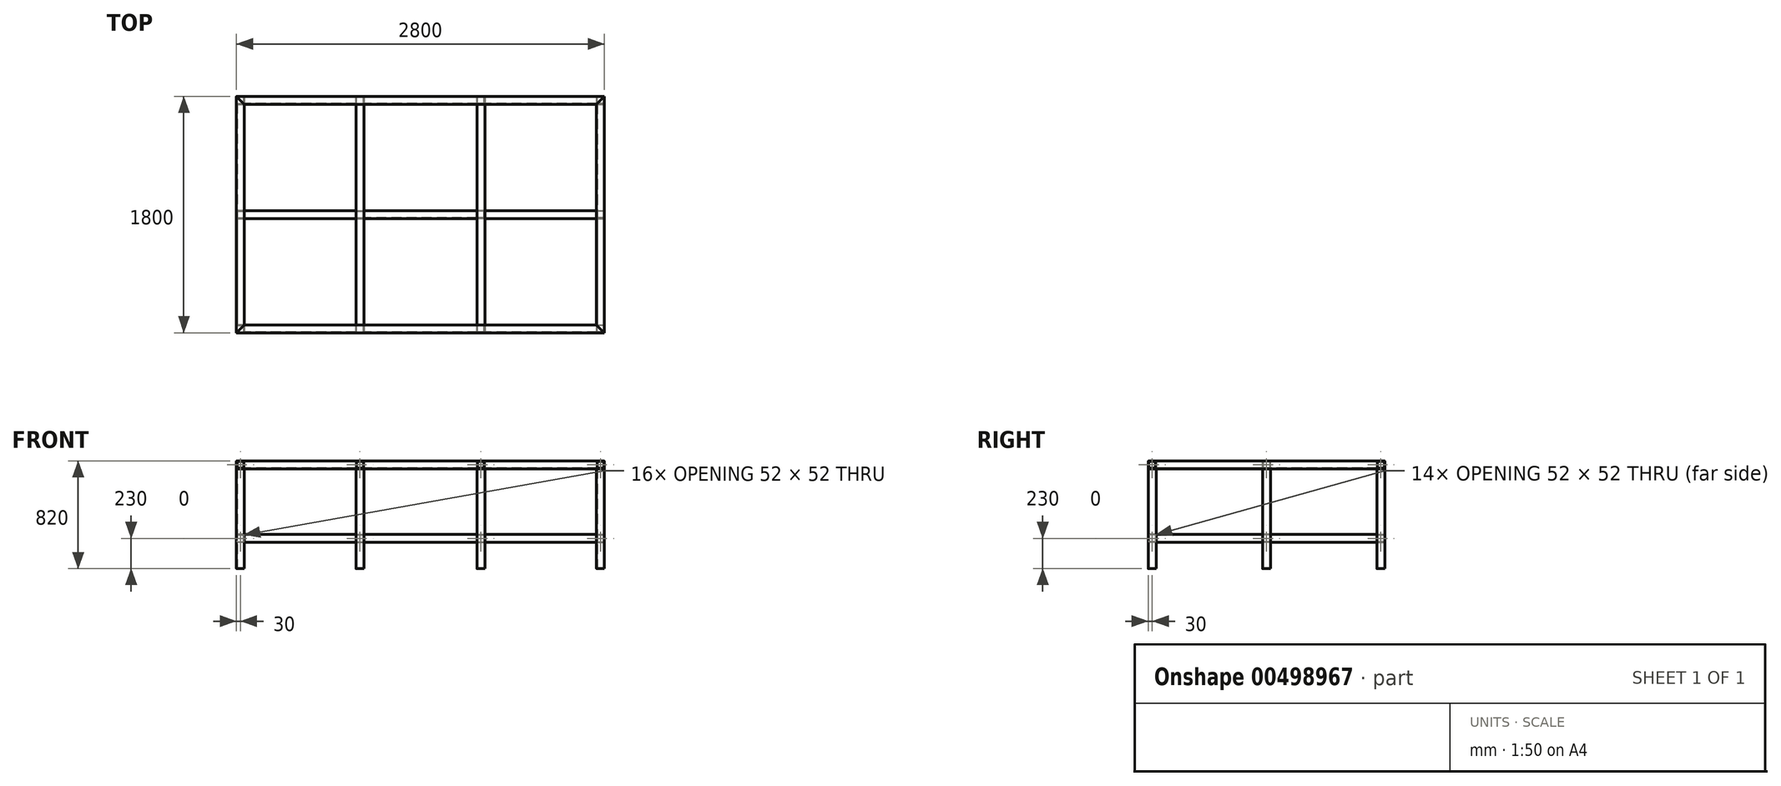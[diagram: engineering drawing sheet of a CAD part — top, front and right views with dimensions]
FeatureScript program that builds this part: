
annotation { "Feature Type Name" : "Feature", "Feature Type Description" : "" }
export const myFeature = defineFeature(function(context is Context, id is Id, definition is map)
    precondition{}
    {
        {
            var Q0;
            Q0=qCreatedBy(makeId("Top.planeOp"),FACE);
            var sketch = newSketch(context, id + "F0", { "sketchPlane" : qUnion([Q0])});
            skLineSegment(sketch, "E0", {"start": v(-1400, 900) * mm, "end": v(1400, 900) * mm});
            skLineSegment(sketch, "E1", {"start": v(-1400, 900) * mm, "end": v(-1340, 840) * mm});
            skLineSegment(sketch, "E2", {"start": v(-1340, 840) * mm, "end": v(1340, 840) * mm});
            skLineSegment(sketch, "E3", {"start": v(1340, 840) * mm, "end": v(1400, 900) * mm});
            skSolve(sketch);
        }
        {
            var Q0;
            Q0 = qSketchRegion(id + "F0", true);
            extrude(context, id + "F1", {"entities" : qUnion([Q0]), "depth" : 60 * mm});
        }
        {
            var Q0;
            Q0=qCreatedBy(makeId("Top.planeOp"),FACE);
            var sketch = newSketch(context, id + "F2", { "sketchPlane" : qUnion([Q0])});
            skLineSegment(sketch, "E4", {"start": v(-1340, 840) * mm, "end": v(-1340, -840) * mm});
            skLineSegment(sketch, "E5", {"start": v(-1340, -840) * mm, "end": v(-1400, -900) * mm});
            skLineSegment(sketch, "E6", {"start": v(-1400, -900) * mm, "end": v(-1400, 900) * mm});
            skLineSegment(sketch, "E7", {"start": v(-1400, 900) * mm, "end": v(-1340, 840) * mm});
            skSolve(sketch);
        }
        {
            var Q0;
            Q0 = qSketchRegion(id + "F2", true);
            extrude(context, id + "F3", {"entities" : qUnion([Q0]), "depth" : 60 * mm});
        }
        {
            var Q0;
            Q0=qCreatedBy(makeId("Top.planeOp"),FACE);
            var sketch = newSketch(context, id + "F4", { "sketchPlane" : qUnion([Q0])});
            skLineSegment(sketch, "E8", {"start": v(-1400, -900) * mm, "end": v(1400, -900) * mm});
            skLineSegment(sketch, "E9", {"start": v(1400, -900) * mm, "end": v(1340, -840) * mm});
            skLineSegment(sketch, "E10", {"start": v(1340, -840) * mm, "end": v(-1340, -840) * mm});
            skLineSegment(sketch, "E11", {"start": v(-1340, -840) * mm, "end": v(-1400, -900) * mm});
            skSolve(sketch);
        }
        {
            var Q0;
            Q0=makeQuery(id+"F4.imprint","IMPRINT",FACE,{"disambiguationData":[TD([[makeQuery(id+"F4.imprint","IMPRINT",EDGE,{"derivedFrom":sQuery(id+"F4.wireOp",EDGE,"E8")}),1.0]])]});
            extrude(context, id + "F5", {"entities" : qUnion([Q0]), "depth" : 60 * mm});
        }
        {
            var Q0;
            Q0=qCreatedBy(makeId("Top.planeOp"),FACE);
            var sketch = newSketch(context, id + "F6", { "sketchPlane" : qUnion([Q0])});
            skLineSegment(sketch, "E12", {"start": v(1400, 900) * mm, "end": v(1400, -900) * mm});
            skLineSegment(sketch, "E13", {"start": v(1400, -900) * mm, "end": v(1340, -840) * mm});
            skLineSegment(sketch, "E14", {"start": v(1340, -840) * mm, "end": v(1340, 840) * mm});
            skLineSegment(sketch, "E15", {"start": v(1340, 840) * mm, "end": v(1400, 900) * mm});
            skSolve(sketch);
        }
        {
            var Q0;
            Q0 = qSketchRegion(id + "F6", true);
            extrude(context, id + "F7", {"entities" : qUnion([Q0]), "depth" : 60 * mm});
        }
        {
            var Q0;
            Q0=makeQuery(id+"F1.opExtrude","SWEPT_FACE",FACE,{"disambiguationData":[OSD([sQuery(id+"F0.wireOp",EDGE,"E2")])]});
            var sketch = newSketch(context, id + "F8", { "sketchPlane" : qUnion([Q0])});
            skLineSegment(sketch, "E16.bottom", {"start": v(-1400, 60) * mm, "end": v(-1340, 60) * mm, "construction": true});
            skLineSegment(sketch, "E16.top", {"start": v(-1400, 0) * mm, "end": v(-1340, 0) * mm, "construction": true});
            skLineSegment(sketch, "E16.left", {"start": v(-1400, 60) * mm, "end": v(-1400, 0) * mm, "construction": true});
            skLineSegment(sketch, "E16.right", {"start": v(-1340, 60) * mm, "end": v(-1340, 0) * mm, "construction": true});
            skLineSegment(sketch, "E17.MirrorCS", {"start": v(1400, 60) * mm, "end": v(1340, 60) * mm, "construction": true});
            skLineSegment(sketch, "E18.MirrorCS", {"start": v(1400, 0) * mm, "end": v(1340, 0) * mm, "construction": true});
            skLineSegment(sketch, "E19.MirrorCS", {"start": v(1400, 60) * mm, "end": v(1400, 0) * mm, "construction": true});
            skLineSegment(sketch, "E20.MirrorCS", {"start": v(1340, 60) * mm, "end": v(1340, 0) * mm, "construction": true});
            skLineSegment(sketch, "E21.bottom", {"start": v(-490, 60) * mm, "end": v(-430, 60) * mm});
            skLineSegment(sketch, "E21.top", {"start": v(-490, 0) * mm, "end": v(-430, 0) * mm});
            skLineSegment(sketch, "E21.left", {"start": v(-490, 60) * mm, "end": v(-490, 0) * mm});
            skLineSegment(sketch, "E21.right", {"start": v(-430, 60) * mm, "end": v(-430, 0) * mm});
            skLineSegment(sketch, "E22.bottom", {"start": v(430, 60) * mm, "end": v(490, 60) * mm});
            skLineSegment(sketch, "E22.top", {"start": v(430, 0) * mm, "end": v(490, 0) * mm});
            skLineSegment(sketch, "E22.left", {"start": v(430, 60) * mm, "end": v(430, 0) * mm});
            skLineSegment(sketch, "E22.right", {"start": v(490, 60) * mm, "end": v(490, 0) * mm});
            skSolve(sketch);
        }
        {
            var Q0;
            Q0 = qSketchRegion(id + "F8", true);
            var Q1;
            Q1=makeQuery(id+"F5.opExtrude","SWEPT_FACE",FACE,{"disambiguationData":[OSD([sQuery(id+"F4.wireOp",EDGE,"E10")])]});
            extrude(context, id + "F9", {"entities" : qUnion([Q0]), "endBound" : BoundingType.UP_TO_SURFACE, "endBoundEntityFace" : qUnion([Q1]), "depth" : 25 * mm});
        }
        {
            var Q0;
            Q0=makeQuery(id+"F3.opExtrude","SWEPT_FACE",FACE,{"disambiguationData":[OSD([sQuery(id+"F2.wireOp",EDGE,"E4")])]});
            var sketch = newSketch(context, id + "F10", { "sketchPlane" : qUnion([Q0])});
            skLineSegment(sketch, "E23.bottom", {"start": v(-30, 60) * mm, "end": v(30, 60) * mm});
            skLineSegment(sketch, "E23.top", {"start": v(-30, 0) * mm, "end": v(30, 0) * mm});
            skLineSegment(sketch, "E23.left", {"start": v(-30, 60) * mm, "end": v(-30, 0) * mm});
            skLineSegment(sketch, "E23.right", {"start": v(30, 60) * mm, "end": v(30, 0) * mm});
            skSolve(sketch);
        }
        {
            var Q0;
            Q0 = qSketchRegion(id + "F10", true);
            extrude(context, id + "F11", {"entities" : qUnion([Q0]), "endBound" : BoundingType.UP_TO_NEXT, "depth" : 25 * mm});
        }
        {
            var Q0;
            Q0=makeQuery(id+"F9.opExtrude","SWEPT_FACE",FACE,{"disambiguationData":[OSD([sQuery(id+"F8.wireOp",EDGE,"E21.right")])]});
            var sketch = newSketch(context, id + "F12", { "sketchPlane" : qUnion([Q0])});
            skSolve(sketch);
        }
        {
            var Q0;
            {var subQ0=sQuery(id+"F8.wireOp",EDGE,"E21.right");Q0=makeQuery(id+"F12.imprint","IMPRINT",FACE,{"disambiguationData":[TD([[makeQuery(id+"F12.imprint","IMPRINT",EDGE,{"derivedFrom":makeQuery(id+"F9.opExtrude","CAP_EDGE",EDGE,{"disambiguationData":[OSD([subQ0])],"isStart":true})}),-1.0]])]});}
            var sketch = newSketch(context, id + "F13", { "sketchPlane" : qUnion([Q0])});
            skLineSegment(sketch, "E24.bottom", {"start": v(-30, 60) * mm, "end": v(30, 60) * mm});
            skLineSegment(sketch, "E24.top", {"start": v(-30, 0) * mm, "end": v(30, 0) * mm});
            skLineSegment(sketch, "E24.left", {"start": v(-30, 60) * mm, "end": v(-30, 0) * mm});
            skLineSegment(sketch, "E24.right", {"start": v(30, 60) * mm, "end": v(30, 0) * mm});
            skSolve(sketch);
        }
        {
            var Q0;
            Q0 = qSketchRegion(id + "F13", true);
            var Q1;
            Q1=makeQuery(id+"F9.opExtrude","SWEPT_FACE",FACE,{"disambiguationData":[OSD([sQuery(id+"F8.wireOp",EDGE,"E22.left")])]});
            extrude(context, id + "F14", {"entities" : qUnion([Q0]), "endBound" : BoundingType.UP_TO_SURFACE, "endBoundEntityFace" : qUnion([Q1]), "depth" : 25 * mm});
        }
        {
            var Q0;
            Q0=makeQuery(id+"F9.opExtrude","SWEPT_FACE",FACE,{"disambiguationData":[OSD([sQuery(id+"F8.wireOp",EDGE,"E22.right")])]});
            var sketch = newSketch(context, id + "F15", { "sketchPlane" : qUnion([Q0])});
            skSolve(sketch);
        }
        {
            var Q0;
            {var subQ0=sQuery(id+"F8.wireOp",EDGE,"E22.right");Q0=makeQuery(id+"F15.imprint","IMPRINT",FACE,{"disambiguationData":[TD([[makeQuery(id+"F15.imprint","IMPRINT",EDGE,{"derivedFrom":makeQuery(id+"F9.opExtrude","CAP_EDGE",EDGE,{"disambiguationData":[OSD([subQ0])],"isStart":true})}),-1.0]])]});}
            var sketch = newSketch(context, id + "F16", { "sketchPlane" : qUnion([Q0])});
            skLineSegment(sketch, "E25.bottom", {"start": v(-30, 60) * mm, "end": v(30, 60) * mm});
            skLineSegment(sketch, "E25.top", {"start": v(-30, 0) * mm, "end": v(30, 0) * mm});
            skLineSegment(sketch, "E25.left", {"start": v(-30, 60) * mm, "end": v(-30, 0) * mm});
            skLineSegment(sketch, "E25.right", {"start": v(30, 60) * mm, "end": v(30, 0) * mm});
            skSolve(sketch);
        }
        {
            var Q0;
            Q0 = qSketchRegion(id + "F16", true);
            var Q1;
            Q1=makeQuery(id+"F7.opExtrude","SWEPT_FACE",FACE,{"disambiguationData":[OSD([sQuery(id+"F6.wireOp",EDGE,"E14")])]});
            extrude(context, id + "F17", {"entities" : qUnion([Q0]), "endBound" : BoundingType.UP_TO_SURFACE, "endBoundEntityFace" : qUnion([Q1]), "depth" : 25 * mm});
        }
        {
            var Q0;
            Q0=makeQuery(id+"F5.opExtrude","CAP_FACE",FACE,{"disambiguationData":[OSD([sQuery(id+"F4.wireOp",EDGE,"E8"),sQuery(id+"F4.wireOp",EDGE,"E9"),sQuery(id+"F4.wireOp",EDGE,"E10"),sQuery(id+"F4.wireOp",EDGE,"E11")])],"isStart":true});
            var sketch = newSketch(context, id + "F18", { "sketchPlane" : qUnion([Q0])});
            skLineSegment(sketch, "E26.bottom", {"start": v(-1340, 840) * mm, "end": v(-1400, 840) * mm});
            skLineSegment(sketch, "E26.top", {"start": v(-1340, 900) * mm, "end": v(-1400, 900) * mm});
            skLineSegment(sketch, "E26.left", {"start": v(-1340, 840) * mm, "end": v(-1340, 900) * mm});
            skLineSegment(sketch, "E26.right", {"start": v(-1400, 840) * mm, "end": v(-1400, 900) * mm});
            skLineSegment(sketch, "E27.bottom", {"start": v(-490, 840) * mm, "end": v(-430, 840) * mm});
            skLineSegment(sketch, "E27.top", {"start": v(-490, 900) * mm, "end": v(-430, 900) * mm});
            skLineSegment(sketch, "E27.left", {"start": v(-490, 840) * mm, "end": v(-490, 900) * mm});
            skLineSegment(sketch, "E27.right", {"start": v(-430, 840) * mm, "end": v(-430, 900) * mm});
            skLineSegment(sketch, "E28.bottom", {"start": v(-1340, 30) * mm, "end": v(-1400, 30) * mm});
            skLineSegment(sketch, "E28.top", {"start": v(-1340, -30) * mm, "end": v(-1400, -30) * mm});
            skLineSegment(sketch, "E28.left", {"start": v(-1340, 30) * mm, "end": v(-1340, -30) * mm});
            skLineSegment(sketch, "E28.right", {"start": v(-1400, 30) * mm, "end": v(-1400, -30) * mm});
            skLineSegment(sketch, "E29.bottom", {"start": v(-490, 30) * mm, "end": v(-430, 30) * mm});
            skLineSegment(sketch, "E29.top", {"start": v(-490, -30) * mm, "end": v(-430, -30) * mm});
            skLineSegment(sketch, "E29.left", {"start": v(-490, 30) * mm, "end": v(-490, -30) * mm});
            skLineSegment(sketch, "E29.right", {"start": v(-430, 30) * mm, "end": v(-430, -30) * mm});
            skLineSegment(sketch, "E30.bottom", {"start": v(-1340, -900) * mm, "end": v(-1400, -900) * mm});
            skLineSegment(sketch, "E30.top", {"start": v(-1340, -840) * mm, "end": v(-1400, -840) * mm});
            skLineSegment(sketch, "E30.left", {"start": v(-1340, -900) * mm, "end": v(-1340, -840) * mm});
            skLineSegment(sketch, "E30.right", {"start": v(-1400, -900) * mm, "end": v(-1400, -840) * mm});
            skLineSegment(sketch, "E31.bottom", {"start": v(-430, -840) * mm, "end": v(-490, -840) * mm});
            skLineSegment(sketch, "E31.top", {"start": v(-430, -900) * mm, "end": v(-490, -900) * mm});
            skLineSegment(sketch, "E31.left", {"start": v(-430, -840) * mm, "end": v(-430, -900) * mm});
            skLineSegment(sketch, "E31.right", {"start": v(-490, -840) * mm, "end": v(-490, -900) * mm});
            skLineSegment(sketch, "E32.MirrorCS", {"start": v(490, 30) * mm, "end": v(430, 30) * mm});
            skLineSegment(sketch, "E33.MirrorCS", {"start": v(1400, 30) * mm, "end": v(1400, -30) * mm});
            skLineSegment(sketch, "E34.MirrorCS", {"start": v(1340, 30) * mm, "end": v(1340, -30) * mm});
            skLineSegment(sketch, "E35.MirrorCS", {"start": v(1340, -30) * mm, "end": v(1400, -30) * mm});
            skLineSegment(sketch, "E36.MirrorCS", {"start": v(430, -840) * mm, "end": v(430, -900) * mm});
            skLineSegment(sketch, "E37.MirrorCS", {"start": v(430, -840) * mm, "end": v(490, -840) * mm});
            skLineSegment(sketch, "E38.MirrorCS", {"start": v(1340, -900) * mm, "end": v(1340, -840) * mm});
            skLineSegment(sketch, "E39.MirrorCS", {"start": v(1340, -900) * mm, "end": v(1400, -900) * mm});
            skLineSegment(sketch, "E40.MirrorCS", {"start": v(1340, 30) * mm, "end": v(1400, 30) * mm});
            skLineSegment(sketch, "E41.MirrorCS", {"start": v(430, 840) * mm, "end": v(430, 900) * mm});
            skLineSegment(sketch, "E42.MirrorCS", {"start": v(490, 840) * mm, "end": v(490, 900) * mm});
            skLineSegment(sketch, "E43.MirrorCS", {"start": v(490, 900) * mm, "end": v(430, 900) * mm});
            skLineSegment(sketch, "E44.MirrorCS", {"start": v(490, 840) * mm, "end": v(430, 840) * mm});
            skLineSegment(sketch, "E45.MirrorCS", {"start": v(1400, 840) * mm, "end": v(1400, 900) * mm});
            skLineSegment(sketch, "E46.MirrorCS", {"start": v(1340, 840) * mm, "end": v(1340, 900) * mm});
            skLineSegment(sketch, "E47.MirrorCS", {"start": v(430, 30) * mm, "end": v(430, -30) * mm});
            skLineSegment(sketch, "E48.MirrorCS", {"start": v(1340, 900) * mm, "end": v(1400, 900) * mm});
            skLineSegment(sketch, "E49.MirrorCS", {"start": v(490, 30) * mm, "end": v(490, -30) * mm});
            skLineSegment(sketch, "E50.MirrorCS", {"start": v(1340, 840) * mm, "end": v(1400, 840) * mm});
            skLineSegment(sketch, "E51.MirrorCS", {"start": v(490, -30) * mm, "end": v(430, -30) * mm});
            skLineSegment(sketch, "E52.MirrorCS", {"start": v(490, -840) * mm, "end": v(490, -900) * mm});
            skLineSegment(sketch, "E53.MirrorCS", {"start": v(430, -900) * mm, "end": v(490, -900) * mm});
            skLineSegment(sketch, "E54.MirrorCS", {"start": v(1400, -900) * mm, "end": v(1400, -840) * mm});
            skLineSegment(sketch, "E55.MirrorCS", {"start": v(1340, -840) * mm, "end": v(1400, -840) * mm});
            skSolve(sketch);
        }
        {
            var Q0;
            Q0 = qSketchRegion(id + "F18", true);
            extrude(context, id + "F19", {"entities" : qUnion([Q0]), "depth" : 760 * mm});
        }
        {
            var Q0;
            Q0=makeQuery(id+"F19.opExtrude","SWEPT_FACE",FACE,{"disambiguationData":[OSD([sQuery(id+"F18.wireOp",EDGE,"E26.top")])]});
            var sketch = newSketch(context, id + "F20", { "sketchPlane" : qUnion([Q0])});
            skLineSegment(sketch, "E56.bottom", {"start": v(-1340, -500) * mm, "end": v(-490, -500) * mm});
            skLineSegment(sketch, "E56.top", {"start": v(-1340, -560) * mm, "end": v(-490, -560) * mm});
            skLineSegment(sketch, "E56.left", {"start": v(-1340, -500) * mm, "end": v(-1340, -560) * mm});
            skLineSegment(sketch, "E56.right", {"start": v(-490, -500) * mm, "end": v(-490, -560) * mm});
            skLineSegment(sketch, "E57.bottom", {"start": v(-430, -500) * mm, "end": v(430, -500) * mm});
            skLineSegment(sketch, "E57.top", {"start": v(-430, -560) * mm, "end": v(430, -560) * mm});
            skLineSegment(sketch, "E57.left", {"start": v(-430, -500) * mm, "end": v(-430, -560) * mm});
            skLineSegment(sketch, "E57.right", {"start": v(430, -500) * mm, "end": v(430, -560) * mm});
            skLineSegment(sketch, "E58.bottom", {"start": v(490, -500) * mm, "end": v(1340, -500) * mm});
            skLineSegment(sketch, "E58.top", {"start": v(490, -560) * mm, "end": v(1340, -560) * mm});
            skLineSegment(sketch, "E58.left", {"start": v(490, -500) * mm, "end": v(490, -560) * mm});
            skLineSegment(sketch, "E58.right", {"start": v(1340, -500) * mm, "end": v(1340, -560) * mm});
            skSolve(sketch);
        }
        {
            var Q0;
            Q0 = qSketchRegion(id + "F20", true);
            extrude(context, id + "F21", {"entities" : qUnion([Q0]), "oppositeDirection" : true, "depth" : 60 * mm});
        }
        {
            var Q0;
            Q0=makeQuery(id+"F19.opExtrude","SWEPT_FACE",FACE,{"disambiguationData":[OSD([sQuery(id+"F18.wireOp",EDGE,"E28.bottom")])]});
            var sketch = newSketch(context, id + "F22", { "sketchPlane" : qUnion([Q0])});
            skLineSegment(sketch, "E59.bottom", {"start": v(-1340, -500) * mm, "end": v(-490, -500) * mm});
            skLineSegment(sketch, "E59.top", {"start": v(-1340, -560) * mm, "end": v(-490, -560) * mm});
            skLineSegment(sketch, "E59.left", {"start": v(-1340, -500) * mm, "end": v(-1340, -560) * mm});
            skLineSegment(sketch, "E59.right", {"start": v(-490, -500) * mm, "end": v(-490, -560) * mm});
            skLineSegment(sketch, "E60.bottom", {"start": v(-430, -500) * mm, "end": v(430, -500) * mm});
            skLineSegment(sketch, "E60.top", {"start": v(-430, -560) * mm, "end": v(430, -560) * mm});
            skLineSegment(sketch, "E60.left", {"start": v(-430, -500) * mm, "end": v(-430, -560) * mm});
            skLineSegment(sketch, "E60.right", {"start": v(430, -500) * mm, "end": v(430, -560) * mm});
            skLineSegment(sketch, "E61.bottom", {"start": v(490, -500) * mm, "end": v(1340, -500) * mm});
            skLineSegment(sketch, "E61.top", {"start": v(490, -560) * mm, "end": v(1340, -560) * mm});
            skLineSegment(sketch, "E61.left", {"start": v(490, -500) * mm, "end": v(490, -560) * mm});
            skLineSegment(sketch, "E61.right", {"start": v(1340, -500) * mm, "end": v(1340, -560) * mm});
            skSolve(sketch);
        }
        {
            var Q0;
            Q0=makeQuery(id+"F22.imprint","IMPRINT",FACE,{"disambiguationData":[TD([[makeQuery(id+"F22.imprint","IMPRINT",EDGE,{"derivedFrom":sQuery(id+"F22.wireOp",EDGE,"E59.bottom")}),-1.0]])]});
            var Q1;
            Q1=makeQuery(id+"F22.imprint","IMPRINT",FACE,{"disambiguationData":[TD([[makeQuery(id+"F22.imprint","IMPRINT",EDGE,{"derivedFrom":sQuery(id+"F22.wireOp",EDGE,"E60.bottom")}),-1.0]])]});
            var Q2;
            Q2=makeQuery(id+"F22.imprint","IMPRINT",FACE,{"disambiguationData":[TD([[makeQuery(id+"F22.imprint","IMPRINT",EDGE,{"derivedFrom":sQuery(id+"F22.wireOp",EDGE,"E61.bottom")}),-1.0]])]});
            extrude(context, id + "F23", {"entities" : qUnion([Q0, Q1, Q2]), "oppositeDirection" : true, "depth" : 60 * mm});
        }
        {
            var Q0;
            Q0=makeQuery(id+"F19.opExtrude","SWEPT_FACE",FACE,{"disambiguationData":[OSD([sQuery(id+"F18.wireOp",EDGE,"E30.bottom")])]});
            var sketch = newSketch(context, id + "F24", { "sketchPlane" : qUnion([Q0])});
            skLineSegment(sketch, "E62.bottom", {"start": v(-1340, -560) * mm, "end": v(-490, -560) * mm});
            skLineSegment(sketch, "E62.top", {"start": v(-1340, -500) * mm, "end": v(-490, -500) * mm});
            skLineSegment(sketch, "E62.left", {"start": v(-1340, -560) * mm, "end": v(-1340, -500) * mm});
            skLineSegment(sketch, "E62.right", {"start": v(-490, -560) * mm, "end": v(-490, -500) * mm});
            skLineSegment(sketch, "E63.bottom", {"start": v(-430, -560) * mm, "end": v(430, -560) * mm});
            skLineSegment(sketch, "E63.top", {"start": v(-430, -500) * mm, "end": v(430, -500) * mm});
            skLineSegment(sketch, "E63.left", {"start": v(-430, -560) * mm, "end": v(-430, -500) * mm});
            skLineSegment(sketch, "E63.right", {"start": v(430, -560) * mm, "end": v(430, -500) * mm});
            skLineSegment(sketch, "E64.bottom", {"start": v(490, -560) * mm, "end": v(1340, -560) * mm});
            skLineSegment(sketch, "E64.top", {"start": v(490, -500) * mm, "end": v(1340, -500) * mm});
            skLineSegment(sketch, "E64.left", {"start": v(490, -560) * mm, "end": v(490, -500) * mm});
            skLineSegment(sketch, "E64.right", {"start": v(1340, -560) * mm, "end": v(1340, -500) * mm});
            skSolve(sketch);
        }
        {
            var Q0;
            Q0 = qSketchRegion(id + "F24", true);
            extrude(context, id + "F25", {"entities" : qUnion([Q0]), "oppositeDirection" : true, "depth" : 60 * mm});
        }
        {
            var Q0;
            Q0=makeQuery(id+"F19.opExtrude","SWEPT_FACE",FACE,{"disambiguationData":[OSD([sQuery(id+"F18.wireOp",EDGE,"E45.MirrorCS")])]});
            var sketch = newSketch(context, id + "F26", { "sketchPlane" : qUnion([Q0])});
            skLineSegment(sketch, "E65.bottom", {"start": v(-840, -500) * mm, "end": v(-30, -500) * mm});
            skLineSegment(sketch, "E65.top", {"start": v(-840, -560) * mm, "end": v(-30, -560) * mm});
            skLineSegment(sketch, "E65.left", {"start": v(-840, -500) * mm, "end": v(-840, -560) * mm});
            skLineSegment(sketch, "E65.right", {"start": v(-30, -500) * mm, "end": v(-30, -560) * mm});
            skLineSegment(sketch, "E66.bottom", {"start": v(30, -500) * mm, "end": v(840, -500) * mm});
            skLineSegment(sketch, "E66.top", {"start": v(30, -560) * mm, "end": v(840, -560) * mm});
            skLineSegment(sketch, "E66.left", {"start": v(30, -500) * mm, "end": v(30, -560) * mm});
            skLineSegment(sketch, "E66.right", {"start": v(840, -500) * mm, "end": v(840, -560) * mm});
            skSolve(sketch);
        }
        {
            var Q0;
            Q0 = qSketchRegion(id + "F26", true);
            extrude(context, id + "F27", {"entities" : qUnion([Q0]), "oppositeDirection" : true, "depth" : 60 * mm});
        }
        {
            var Q0;
            Q0=makeQuery(id+"F19.opExtrude","SWEPT_FACE",FACE,{"disambiguationData":[OSD([sQuery(id+"F18.wireOp",EDGE,"E42.MirrorCS")])]});
            var sketch = newSketch(context, id + "F28", { "sketchPlane" : qUnion([Q0])});
            skLineSegment(sketch, "E67.bottom", {"start": v(-840, -500) * mm, "end": v(-30, -500) * mm});
            skLineSegment(sketch, "E67.top", {"start": v(-840, -560) * mm, "end": v(-30, -560) * mm});
            skLineSegment(sketch, "E67.left", {"start": v(-840, -500) * mm, "end": v(-840, -560) * mm});
            skLineSegment(sketch, "E67.right", {"start": v(-30, -500) * mm, "end": v(-30, -560) * mm});
            skLineSegment(sketch, "E68.bottom", {"start": v(30, -500) * mm, "end": v(840, -500) * mm});
            skLineSegment(sketch, "E68.top", {"start": v(30, -560) * mm, "end": v(840, -560) * mm});
            skLineSegment(sketch, "E68.left", {"start": v(30, -500) * mm, "end": v(30, -560) * mm});
            skLineSegment(sketch, "E68.right", {"start": v(840, -500) * mm, "end": v(840, -560) * mm});
            skSolve(sketch);
        }
        {
            var Q0;
            Q0 = qSketchRegion(id + "F28", true);
            extrude(context, id + "F29", {"entities" : qUnion([Q0]), "oppositeDirection" : true, "depth" : 60 * mm});
        }
        {
            var Q0;
            Q0=makeQuery(id+"F19.opExtrude","SWEPT_FACE",FACE,{"disambiguationData":[OSD([sQuery(id+"F18.wireOp",EDGE,"E27.right")])]});
            var sketch = newSketch(context, id + "F30", { "sketchPlane" : qUnion([Q0])});
            skLineSegment(sketch, "E69.bottom", {"start": v(-840, -500) * mm, "end": v(-30, -500) * mm});
            skLineSegment(sketch, "E69.top", {"start": v(-840, -560) * mm, "end": v(-30, -560) * mm});
            skLineSegment(sketch, "E69.left", {"start": v(-840, -500) * mm, "end": v(-840, -560) * mm});
            skLineSegment(sketch, "E69.right", {"start": v(-30, -500) * mm, "end": v(-30, -560) * mm});
            skLineSegment(sketch, "E70.bottom", {"start": v(30, -500) * mm, "end": v(840, -500) * mm});
            skLineSegment(sketch, "E70.top", {"start": v(30, -560) * mm, "end": v(840, -560) * mm});
            skLineSegment(sketch, "E70.left", {"start": v(30, -500) * mm, "end": v(30, -560) * mm});
            skLineSegment(sketch, "E70.right", {"start": v(840, -500) * mm, "end": v(840, -560) * mm});
            skSolve(sketch);
        }
        {
            var Q0;
            Q0 = qSketchRegion(id + "F30", true);
            extrude(context, id + "F31", {"entities" : qUnion([Q0]), "oppositeDirection" : true, "depth" : 60 * mm});
        }
        {
            var Q0;
            Q0=makeQuery(id+"F19.opExtrude","SWEPT_FACE",FACE,{"disambiguationData":[OSD([sQuery(id+"F18.wireOp",EDGE,"E30.right")])]});
            var sketch = newSketch(context, id + "F32", { "sketchPlane" : qUnion([Q0])});
            skLineSegment(sketch, "E71.bottom", {"start": v(840, -500) * mm, "end": v(30, -500) * mm});
            skLineSegment(sketch, "E71.top", {"start": v(840, -560) * mm, "end": v(30, -560) * mm});
            skLineSegment(sketch, "E71.left", {"start": v(840, -500) * mm, "end": v(840, -560) * mm});
            skLineSegment(sketch, "E71.right", {"start": v(30, -500) * mm, "end": v(30, -560) * mm});
            skLineSegment(sketch, "E72.bottom", {"start": v(-30, -500) * mm, "end": v(-840, -500) * mm});
            skLineSegment(sketch, "E72.top", {"start": v(-30, -560) * mm, "end": v(-840, -560) * mm});
            skLineSegment(sketch, "E72.left", {"start": v(-30, -500) * mm, "end": v(-30, -560) * mm});
            skLineSegment(sketch, "E72.right", {"start": v(-840, -500) * mm, "end": v(-840, -560) * mm});
            skSolve(sketch);
        }
        {
            var Q0;
            Q0 = qSketchRegion(id + "F32", true);
            extrude(context, id + "F33", {"entities" : qUnion([Q0]), "oppositeDirection" : true, "depth" : 60 * mm});
        }
        {
            var Q0;
            Q0=makeQuery(id+"F19.opExtrude","CAP_FACE",FACE,{"disambiguationData":[OSD([sQuery(id+"F18.wireOp",EDGE,"E45.MirrorCS"),sQuery(id+"F18.wireOp",EDGE,"E46.MirrorCS"),sQuery(id+"F18.wireOp",EDGE,"E48.MirrorCS"),sQuery(id+"F18.wireOp",EDGE,"E50.MirrorCS")])],"isStart":false});
            var sketch = newSketch(context, id + "F34", { "sketchPlane" : qUnion([Q0])});
            skLineSegment(sketch, "E73.bottom", {"start": v(1396, 896) * mm, "end": v(1344, 896) * mm});
            skLineSegment(sketch, "E73.top", {"start": v(1396, 844) * mm, "end": v(1344, 844) * mm});
            skLineSegment(sketch, "E73.left", {"start": v(1396, 896) * mm, "end": v(1396, 844) * mm});
            skLineSegment(sketch, "E73.right", {"start": v(1344, 896) * mm, "end": v(1344, 844) * mm});
            skLineSegment(sketch, "E74.bottom", {"start": v(1396, 26) * mm, "end": v(1344, 26) * mm});
            skLineSegment(sketch, "E74.top", {"start": v(1396, -26) * mm, "end": v(1344, -26) * mm});
            skLineSegment(sketch, "E74.left", {"start": v(1396, 26) * mm, "end": v(1396, -26) * mm});
            skLineSegment(sketch, "E74.right", {"start": v(1344, 26) * mm, "end": v(1344, -26) * mm});
            skLineSegment(sketch, "E75.bottom", {"start": v(486, 896) * mm, "end": v(434, 896) * mm});
            skLineSegment(sketch, "E75.top", {"start": v(486, 844) * mm, "end": v(434, 844) * mm});
            skLineSegment(sketch, "E75.left", {"start": v(486, 896) * mm, "end": v(486, 844) * mm});
            skLineSegment(sketch, "E75.right", {"start": v(434, 896) * mm, "end": v(434, 844) * mm});
            skLineSegment(sketch, "E76.bottom", {"start": v(486, 26) * mm, "end": v(434, 26) * mm});
            skLineSegment(sketch, "E76.top", {"start": v(486, -26) * mm, "end": v(434, -26) * mm});
            skLineSegment(sketch, "E76.left", {"start": v(486, 26) * mm, "end": v(486, -26) * mm});
            skLineSegment(sketch, "E76.right", {"start": v(434, 26) * mm, "end": v(434, -26) * mm});
            skLineSegment(sketch, "E77.bottom", {"start": v(486, -844) * mm, "end": v(434, -844) * mm});
            skLineSegment(sketch, "E77.top", {"start": v(486, -896) * mm, "end": v(434, -896) * mm});
            skLineSegment(sketch, "E77.left", {"start": v(486, -844) * mm, "end": v(486, -896) * mm});
            skLineSegment(sketch, "E77.right", {"start": v(434, -844) * mm, "end": v(434, -896) * mm});
            skLineSegment(sketch, "E78.bottom", {"start": v(1396, -844) * mm, "end": v(1344, -844) * mm});
            skLineSegment(sketch, "E78.top", {"start": v(1396, -896) * mm, "end": v(1344, -896) * mm});
            skLineSegment(sketch, "E78.left", {"start": v(1396, -844) * mm, "end": v(1396, -896) * mm});
            skLineSegment(sketch, "E78.right", {"start": v(1344, -844) * mm, "end": v(1344, -896) * mm});
            skLineSegment(sketch, "E79.MirrorCS", {"start": v(-486, -896) * mm, "end": v(-434, -896) * mm});
            skLineSegment(sketch, "E80.MirrorCS", {"start": v(-434, -844) * mm, "end": v(-434, -896) * mm});
            skLineSegment(sketch, "E81.MirrorCS", {"start": v(-486, 896) * mm, "end": v(-434, 896) * mm});
            skLineSegment(sketch, "E82.MirrorCS", {"start": v(-486, 844) * mm, "end": v(-434, 844) * mm});
            skLineSegment(sketch, "E83.MirrorCS", {"start": v(-486, -844) * mm, "end": v(-486, -896) * mm});
            skLineSegment(sketch, "E84.MirrorCS", {"start": v(-1396, -844) * mm, "end": v(-1396, -896) * mm});
            skLineSegment(sketch, "E85.MirrorCS", {"start": v(-1396, 844) * mm, "end": v(-1344, 844) * mm});
            skLineSegment(sketch, "E86.MirrorCS", {"start": v(-486, 896) * mm, "end": v(-486, 844) * mm});
            skLineSegment(sketch, "E87.MirrorCS", {"start": v(-486, -844) * mm, "end": v(-434, -844) * mm});
            skLineSegment(sketch, "E88.MirrorCS", {"start": v(-1396, 26) * mm, "end": v(-1396, -26) * mm});
            skLineSegment(sketch, "E89.MirrorCS", {"start": v(-1396, 896) * mm, "end": v(-1396, 844) * mm});
            skLineSegment(sketch, "E90.MirrorCS", {"start": v(-1396, -896) * mm, "end": v(-1344, -896) * mm});
            skLineSegment(sketch, "E91.MirrorCS", {"start": v(-434, 896) * mm, "end": v(-434, 844) * mm});
            skLineSegment(sketch, "E92.MirrorCS", {"start": v(-1344, 896) * mm, "end": v(-1344, 844) * mm});
            skLineSegment(sketch, "E93.MirrorCS", {"start": v(-486, 26) * mm, "end": v(-486, -26) * mm});
            skLineSegment(sketch, "E94.MirrorCS", {"start": v(-1396, -844) * mm, "end": v(-1344, -844) * mm});
            skLineSegment(sketch, "E95.MirrorCS", {"start": v(-434, 26) * mm, "end": v(-434, -26) * mm});
            skLineSegment(sketch, "E96.MirrorCS", {"start": v(-1344, 26) * mm, "end": v(-1344, -26) * mm});
            skLineSegment(sketch, "E97.MirrorCS", {"start": v(-486, -26) * mm, "end": v(-434, -26) * mm});
            skLineSegment(sketch, "E98.MirrorCS", {"start": v(-1344, -844) * mm, "end": v(-1344, -896) * mm});
            skLineSegment(sketch, "E99.MirrorCS", {"start": v(-1396, -26) * mm, "end": v(-1344, -26) * mm});
            skLineSegment(sketch, "E100.MirrorCS", {"start": v(-1396, 26) * mm, "end": v(-1344, 26) * mm});
            skLineSegment(sketch, "E101.MirrorCS", {"start": v(-1396, 896) * mm, "end": v(-1344, 896) * mm});
            skLineSegment(sketch, "E102.MirrorCS", {"start": v(-486, 26) * mm, "end": v(-434, 26) * mm});
            skSolve(sketch);
        }
        {
            var Q0;
            Q0 = qSketchRegion(id + "F34", true);
            extrude(context, id + "F35", {"entities" : qUnion([Q0]), "operationType" : NewBodyOperationType.REMOVE, "oppositeDirection" : true, "depth" : 760 * mm});
        }
        {
            var Q0;
            Q0=makeQuery(id+"F21.opExtrude","SWEPT_FACE",FACE,{"disambiguationData":[OSD([sQuery(id+"F20.wireOp",EDGE,"E56.left")])]});
            var sketch = newSketch(context, id + "F36", { "sketchPlane" : qUnion([Q0])});
            skLineSegment(sketch, "E103.bottom", {"start": v(844, -504) * mm, "end": v(896, -504) * mm});
            skLineSegment(sketch, "E103.top", {"start": v(844, -556) * mm, "end": v(896, -556) * mm});
            skLineSegment(sketch, "E103.left", {"start": v(844, -504) * mm, "end": v(844, -556) * mm});
            skLineSegment(sketch, "E103.right", {"start": v(896, -504) * mm, "end": v(896, -556) * mm});
            skLineSegment(sketch, "E104.bottom", {"start": v(-26, -504) * mm, "end": v(26, -504) * mm});
            skLineSegment(sketch, "E104.top", {"start": v(-26, -556) * mm, "end": v(26, -556) * mm});
            skLineSegment(sketch, "E104.left", {"start": v(-26, -504) * mm, "end": v(-26, -556) * mm});
            skLineSegment(sketch, "E104.right", {"start": v(26, -504) * mm, "end": v(26, -556) * mm});
            skLineSegment(sketch, "E105.bottom", {"start": v(-896, -504) * mm, "end": v(-844, -504) * mm});
            skLineSegment(sketch, "E105.top", {"start": v(-896, -556) * mm, "end": v(-844, -556) * mm});
            skLineSegment(sketch, "E105.left", {"start": v(-896, -504) * mm, "end": v(-896, -556) * mm});
            skLineSegment(sketch, "E105.right", {"start": v(-844, -504) * mm, "end": v(-844, -556) * mm});
            skSolve(sketch);
        }
        {
            var Q0;
            Q0 = qSketchRegion(id + "F36", true);
            var Q1;
            Q1=makeQuery(id+"F19.opExtrude","SWEPT_FACE",FACE,{"disambiguationData":[OSD([sQuery(id+"F18.wireOp",EDGE,"E27.left")])]});
            extrude(context, id + "F37", {"entities" : qUnion([Q0]), "operationType" : NewBodyOperationType.REMOVE, "endBound" : BoundingType.UP_TO_SURFACE, "oppositeDirection" : true, "endBoundEntityFace" : qUnion([Q1]), "depth" : 25 * mm});
        }
        {
            var Q0;
            Q0=makeQuery(id+"F33.opExtrude","SWEPT_FACE",FACE,{"disambiguationData":[OSD([sQuery(id+"F32.wireOp",EDGE,"E71.left")])]});
            var sketch = newSketch(context, id + "F38", { "sketchPlane" : qUnion([Q0])});
            skLineSegment(sketch, "E106.bottom", {"start": v(-1396, -556) * mm, "end": v(-1344, -556) * mm});
            skLineSegment(sketch, "E106.top", {"start": v(-1396, -504) * mm, "end": v(-1344, -504) * mm});
            skLineSegment(sketch, "E106.left", {"start": v(-1396, -556) * mm, "end": v(-1396, -504) * mm});
            skLineSegment(sketch, "E106.right", {"start": v(-1344, -556) * mm, "end": v(-1344, -504) * mm});
            skSolve(sketch);
        }
        {
            var Q0;
            Q0 = qSketchRegion(id + "F38", true);
            var Q1;
            Q1=makeQuery(id+"F33.opExtrude","SWEPT_FACE",FACE,{"disambiguationData":[OSD([sQuery(id+"F32.wireOp",EDGE,"E71.right")])]});
            extrude(context, id + "F39", {"entities" : qUnion([Q0]), "operationType" : NewBodyOperationType.REMOVE, "endBound" : BoundingType.UP_TO_SURFACE, "oppositeDirection" : true, "endBoundEntityFace" : qUnion([Q1]), "depth" : 25 * mm});
        }
        {
            var Q0;
            Q0=makeQuery(id+"F33.opExtrude","SWEPT_FACE",FACE,{"disambiguationData":[OSD([sQuery(id+"F32.wireOp",EDGE,"E72.right")])]});
            var sketch = newSketch(context, id + "F40", { "sketchPlane" : qUnion([Q0])});
            skLineSegment(sketch, "E107.bottom", {"start": v(1396, -504) * mm, "end": v(1344, -504) * mm});
            skLineSegment(sketch, "E107.top", {"start": v(1396, -556) * mm, "end": v(1344, -556) * mm});
            skLineSegment(sketch, "E107.left", {"start": v(1396, -504) * mm, "end": v(1396, -556) * mm});
            skLineSegment(sketch, "E107.right", {"start": v(1344, -504) * mm, "end": v(1344, -556) * mm});
            skSolve(sketch);
        }
        {
            var Q0;
            Q0 = qSketchRegion(id + "F40", true);
            var Q1;
            Q1=makeQuery(id+"F33.opExtrude","SWEPT_FACE",FACE,{"disambiguationData":[OSD([sQuery(id+"F32.wireOp",EDGE,"E72.left")])]});
            extrude(context, id + "F41", {"entities" : qUnion([Q0]), "operationType" : NewBodyOperationType.REMOVE, "endBound" : BoundingType.UP_TO_SURFACE, "oppositeDirection" : true, "endBoundEntityFace" : qUnion([Q1]), "depth" : 25 * mm});
        }
        {
            var Q0;
            Q0=qCreatedBy(makeId("Front.planeOp"),FACE);
            var sketch = newSketch(context, id + "F42", { "sketchPlane" : qUnion([Q0])});
            skLineSegment(sketch, "E108.bottom", {"start": v(-1396, 56) * mm, "end": v(-1344, 56) * mm});
            skLineSegment(sketch, "E108.top", {"start": v(-1396, 4) * mm, "end": v(-1344, 4) * mm});
            skLineSegment(sketch, "E108.left", {"start": v(-1396, 56) * mm, "end": v(-1396, 4) * mm});
            skLineSegment(sketch, "E108.right", {"start": v(-1344, 56) * mm, "end": v(-1344, 4) * mm});
            skLineSegment(sketch, "E109.bottom", {"start": v(-486, 56) * mm, "end": v(-434, 56) * mm});
            skLineSegment(sketch, "E109.top", {"start": v(-486, 4) * mm, "end": v(-434, 4) * mm});
            skLineSegment(sketch, "E109.left", {"start": v(-486, 56) * mm, "end": v(-486, 4) * mm});
            skLineSegment(sketch, "E109.right", {"start": v(-434, 56) * mm, "end": v(-434, 4) * mm});
            skLineSegment(sketch, "E110.bottom", {"start": v(434, 56) * mm, "end": v(486, 56) * mm});
            skLineSegment(sketch, "E110.top", {"start": v(434, 4) * mm, "end": v(486, 4) * mm});
            skLineSegment(sketch, "E110.left", {"start": v(434, 56) * mm, "end": v(434, 4) * mm});
            skLineSegment(sketch, "E110.right", {"start": v(486, 56) * mm, "end": v(486, 4) * mm});
            skLineSegment(sketch, "E111.bottom", {"start": v(1344, 56) * mm, "end": v(1396, 56) * mm});
            skLineSegment(sketch, "E111.top", {"start": v(1344, 4) * mm, "end": v(1396, 4) * mm});
            skLineSegment(sketch, "E111.left", {"start": v(1344, 56) * mm, "end": v(1344, 4) * mm});
            skLineSegment(sketch, "E111.right", {"start": v(1396, 56) * mm, "end": v(1396, 4) * mm});
            skSolve(sketch);
        }
        {
            var Q0;
            Q0 = qSketchRegion(id + "F42", true);
            extrude(context, id + "F43", {"entities" : qUnion([Q0]), "operationType" : NewBodyOperationType.REMOVE, "endBound" : BoundingType.SYMMETRIC, "oppositeDirection" : true, "depth" : 1800 * mm});
        }
        {
            var Q0;
            Q0=makeQuery(id+"F17.opExtrude","CAP_FACE",FACE,{"disambiguationData":[OSD([sQuery(id+"F16.wireOp",EDGE,"E25.bottom"),sQuery(id+"F16.wireOp",EDGE,"E25.top"),sQuery(id+"F16.wireOp",EDGE,"E25.left"),sQuery(id+"F16.wireOp",EDGE,"E25.right")])],"isStart":false});
            var sketch = newSketch(context, id + "F44", { "sketchPlane" : qUnion([Q0])});
            skLineSegment(sketch, "E112.bottom", {"start": v(-26, 56) * mm, "end": v(26, 56) * mm});
            skLineSegment(sketch, "E112.top", {"start": v(-26, 4) * mm, "end": v(26, 4) * mm});
            skLineSegment(sketch, "E112.left", {"start": v(-26, 56) * mm, "end": v(-26, 4) * mm});
            skLineSegment(sketch, "E112.right", {"start": v(26, 56) * mm, "end": v(26, 4) * mm});
            skSolve(sketch);
        }
        {
            var Q0;
            Q0 = qSketchRegion(id + "F44", true);
            var Q1;
            Q1=makeQuery(id+"F3.opExtrude","SWEPT_FACE",FACE,{"disambiguationData":[OSD([sQuery(id+"F2.wireOp",EDGE,"E4")])]});
            extrude(context, id + "F45", {"entities" : qUnion([Q0]), "operationType" : NewBodyOperationType.REMOVE, "endBound" : BoundingType.UP_TO_SURFACE, "oppositeDirection" : true, "endBoundEntityFace" : qUnion([Q1]), "depth" : 25 * mm});
        }
        {
            var Q0;
            Q0=makeQuery(id+"F31.opExtrude","SWEPT_FACE",FACE,{"disambiguationData":[OSD([sQuery(id+"F30.wireOp",EDGE,"E69.left")])]});
            var sketch = newSketch(context, id + "F46", { "sketchPlane" : qUnion([Q0])});
            skLineSegment(sketch, "E113.bottom", {"start": v(-486, -504) * mm, "end": v(-434, -504) * mm});
            skLineSegment(sketch, "E113.top", {"start": v(-486, -556) * mm, "end": v(-434, -556) * mm});
            skLineSegment(sketch, "E113.left", {"start": v(-486, -504) * mm, "end": v(-486, -556) * mm});
            skLineSegment(sketch, "E113.right", {"start": v(-434, -504) * mm, "end": v(-434, -556) * mm});
            skLineSegment(sketch, "E114.bottom", {"start": v(434, -504) * mm, "end": v(486, -504) * mm});
            skLineSegment(sketch, "E114.top", {"start": v(434, -556) * mm, "end": v(486, -556) * mm});
            skLineSegment(sketch, "E114.left", {"start": v(434, -504) * mm, "end": v(434, -556) * mm});
            skLineSegment(sketch, "E114.right", {"start": v(486, -504) * mm, "end": v(486, -556) * mm});
            skLineSegment(sketch, "E115.bottom", {"start": v(1344, -504) * mm, "end": v(1396, -504) * mm});
            skLineSegment(sketch, "E115.top", {"start": v(1344, -556) * mm, "end": v(1396, -556) * mm});
            skLineSegment(sketch, "E115.left", {"start": v(1344, -504) * mm, "end": v(1344, -556) * mm});
            skLineSegment(sketch, "E115.right", {"start": v(1396, -504) * mm, "end": v(1396, -556) * mm});
            skSolve(sketch);
        }
        {
            var Q0;
            Q0 = qSketchRegion(id + "F46", true);
            var Q1;
            Q1=makeQuery(id+"F23.opExtrude","CAP_FACE",FACE,{"disambiguationData":[OSD([sQuery(id+"F22.wireOp",EDGE,"E60.bottom"),sQuery(id+"F22.wireOp",EDGE,"E60.top"),sQuery(id+"F22.wireOp",EDGE,"E60.left"),sQuery(id+"F22.wireOp",EDGE,"E60.right")])],"isStart":true});
            extrude(context, id + "F47", {"entities" : qUnion([Q0]), "operationType" : NewBodyOperationType.REMOVE, "endBound" : BoundingType.UP_TO_SURFACE, "oppositeDirection" : true, "endBoundEntityFace" : qUnion([Q1]), "depth" : 25 * mm});
        }
        {
            var Q0;
            Q0=makeQuery(id+"F31.opExtrude","SWEPT_FACE",FACE,{"disambiguationData":[OSD([sQuery(id+"F30.wireOp",EDGE,"E70.left")])]});
            var sketch = newSketch(context, id + "F48", { "sketchPlane" : qUnion([Q0])});
            skLineSegment(sketch, "E116.bottom", {"start": v(-486, -504) * mm, "end": v(-434, -504) * mm});
            skLineSegment(sketch, "E116.top", {"start": v(-486, -556) * mm, "end": v(-434, -556) * mm});
            skLineSegment(sketch, "E116.left", {"start": v(-486, -504) * mm, "end": v(-486, -556) * mm});
            skLineSegment(sketch, "E116.right", {"start": v(-434, -504) * mm, "end": v(-434, -556) * mm});
            skLineSegment(sketch, "E117.bottom", {"start": v(434, -504) * mm, "end": v(486, -504) * mm});
            skLineSegment(sketch, "E117.top", {"start": v(434, -556) * mm, "end": v(486, -556) * mm});
            skLineSegment(sketch, "E117.left", {"start": v(434, -504) * mm, "end": v(434, -556) * mm});
            skLineSegment(sketch, "E117.right", {"start": v(486, -504) * mm, "end": v(486, -556) * mm});
            skLineSegment(sketch, "E118.bottom", {"start": v(1344, -504) * mm, "end": v(1396, -504) * mm});
            skLineSegment(sketch, "E118.top", {"start": v(1344, -556) * mm, "end": v(1396, -556) * mm});
            skLineSegment(sketch, "E118.left", {"start": v(1344, -504) * mm, "end": v(1344, -556) * mm});
            skLineSegment(sketch, "E118.right", {"start": v(1396, -504) * mm, "end": v(1396, -556) * mm});
            skSolve(sketch);
        }
        {
            var Q0;
            Q0 = qSketchRegion(id + "F48", true);
            extrude(context, id + "F49", {"entities" : qUnion([Q0]), "operationType" : NewBodyOperationType.REMOVE, "endBound" : BoundingType.UP_TO_NEXT, "oppositeDirection" : true, "depth" : 25 * mm});
        }
        {
            var Q0;
            Q0=makeQuery(id+"F23.opExtrude","SWEPT_FACE",FACE,{"disambiguationData":[OSD([sQuery(id+"F22.wireOp",EDGE,"E60.left")])]});
            var sketch = newSketch(context, id + "F50", { "sketchPlane" : qUnion([Q0])});
            skLineSegment(sketch, "E119.bottom", {"start": v(-26, -504) * mm, "end": v(26, -504) * mm});
            skLineSegment(sketch, "E119.top", {"start": v(-26, -556) * mm, "end": v(26, -556) * mm});
            skLineSegment(sketch, "E119.left", {"start": v(-26, -504) * mm, "end": v(-26, -556) * mm});
            skLineSegment(sketch, "E119.right", {"start": v(26, -504) * mm, "end": v(26, -556) * mm});
            skSolve(sketch);
        }
        {
            var Q0;
            Q0=makeQuery(id+"F50.imprint","IMPRINT",FACE,{"disambiguationData":[TD([[makeQuery(id+"F50.imprint","IMPRINT",EDGE,{"derivedFrom":sQuery(id+"F50.wireOp",EDGE,"E119.bottom")}),-1.0]])]});
            extrude(context, id + "F51", {"entities" : qUnion([Q0]), "operationType" : NewBodyOperationType.REMOVE, "endBound" : BoundingType.UP_TO_NEXT, "oppositeDirection" : true, "depth" : 25 * mm});
        }
        {
            var Q0;
            Q0=makeQuery(id+"F23.opExtrude","SWEPT_FACE",FACE,{"disambiguationData":[OSD([sQuery(id+"F22.wireOp",EDGE,"E61.right")])]});
            var sketch = newSketch(context, id + "F52", { "sketchPlane" : qUnion([Q0])});
            skLineSegment(sketch, "E120.bottom", {"start": v(26, -504) * mm, "end": v(-26, -504) * mm});
            skLineSegment(sketch, "E120.top", {"start": v(26, -556) * mm, "end": v(-26, -556) * mm});
            skLineSegment(sketch, "E120.left", {"start": v(26, -504) * mm, "end": v(26, -556) * mm});
            skLineSegment(sketch, "E120.right", {"start": v(-26, -504) * mm, "end": v(-26, -556) * mm});
            skSolve(sketch);
        }
        {
            var Q0;
            Q0 = qSketchRegion(id + "F52", true);
            extrude(context, id + "F53", {"entities" : qUnion([Q0]), "operationType" : NewBodyOperationType.REMOVE, "endBound" : BoundingType.UP_TO_NEXT, "oppositeDirection" : true, "depth" : 25 * mm});
        }
        {
            var Q0;
            Q0=makeQuery(id+"F21.opExtrude","SWEPT_FACE",FACE,{"disambiguationData":[OSD([sQuery(id+"F20.wireOp",EDGE,"E57.right")])]});
            var sketch = newSketch(context, id + "F54", { "sketchPlane" : qUnion([Q0])});
            skLineSegment(sketch, "E121.bottom", {"start": v(-896, -504) * mm, "end": v(-844, -504) * mm});
            skLineSegment(sketch, "E121.top", {"start": v(-896, -556) * mm, "end": v(-844, -556) * mm});
            skLineSegment(sketch, "E121.left", {"start": v(-896, -504) * mm, "end": v(-896, -556) * mm});
            skLineSegment(sketch, "E121.right", {"start": v(-844, -504) * mm, "end": v(-844, -556) * mm});
            skSolve(sketch);
        }
        {
            var Q0;
            Q0 = qSketchRegion(id + "F54", true);
            extrude(context, id + "F55", {"entities" : qUnion([Q0]), "operationType" : NewBodyOperationType.REMOVE, "endBound" : BoundingType.UP_TO_NEXT, "oppositeDirection" : true, "depth" : 25 * mm});
        }
        {
            var Q0;
            Q0=makeQuery(id+"F21.opExtrude","SWEPT_FACE",FACE,{"disambiguationData":[OSD([sQuery(id+"F20.wireOp",EDGE,"E58.right")])]});
            var sketch = newSketch(context, id + "F56", { "sketchPlane" : qUnion([Q0])});
            skLineSegment(sketch, "E122.bottom", {"start": v(-844, -504) * mm, "end": v(-896, -504) * mm});
            skLineSegment(sketch, "E122.top", {"start": v(-844, -556) * mm, "end": v(-896, -556) * mm});
            skLineSegment(sketch, "E122.left", {"start": v(-844, -504) * mm, "end": v(-844, -556) * mm});
            skLineSegment(sketch, "E122.right", {"start": v(-896, -504) * mm, "end": v(-896, -556) * mm});
            skSolve(sketch);
        }
        {
            var Q0;
            Q0 = qSketchRegion(id + "F56", true);
            extrude(context, id + "F57", {"entities" : qUnion([Q0]), "operationType" : NewBodyOperationType.REMOVE, "endBound" : BoundingType.UP_TO_NEXT, "oppositeDirection" : true, "depth" : 25 * mm});
        }
        {
            var Q0;
            Q0=makeQuery(id+"F25.opExtrude","SWEPT_FACE",FACE,{"disambiguationData":[OSD([sQuery(id+"F24.wireOp",EDGE,"E62.left")])]});
            var sketch = newSketch(context, id + "F58", { "sketchPlane" : qUnion([Q0])});
            skLineSegment(sketch, "E123.bottom", {"start": v(896, -504) * mm, "end": v(844, -504) * mm});
            skLineSegment(sketch, "E123.top", {"start": v(896, -556) * mm, "end": v(844, -556) * mm});
            skLineSegment(sketch, "E123.left", {"start": v(896, -504) * mm, "end": v(896, -556) * mm});
            skLineSegment(sketch, "E123.right", {"start": v(844, -504) * mm, "end": v(844, -556) * mm});
            skSolve(sketch);
        }
        {
            var Q0;
            Q0 = qSketchRegion(id + "F58", true);
            var Q1;
            Q1=makeQuery(id+"F25.opExtrude","SWEPT_FACE",FACE,{"disambiguationData":[OSD([sQuery(id+"F24.wireOp",EDGE,"E63.right")])]});
            extrude(context, id + "F59", {"entities" : qUnion([Q0]), "operationType" : NewBodyOperationType.REMOVE, "endBound" : BoundingType.UP_TO_SURFACE, "oppositeDirection" : true, "endBoundEntityFace" : qUnion([Q1]), "depth" : 25 * mm});
        }
        {
            var Q0;
            Q0=makeQuery(id+"F19.opExtrude","SWEPT_EDGE",EDGE,{"disambiguationData":[OSD([sQuery(id+"F4.wireOp",EDGE,"E9"),sQuery(id+"F18.wireOp",EDGE,"E45.MirrorCS"),sQuery(id+"F18.wireOp",EDGE,"E48.MirrorCS")])]});
            var Q1;
            Q1=makeQuery(id+"F19.opExtrude","SWEPT_EDGE",EDGE,{"disambiguationData":[OSD([sQuery(id+"F4.wireOp",EDGE,"E8"),sQuery(id+"F18.wireOp",EDGE,"E46.MirrorCS"),sQuery(id+"F18.wireOp",EDGE,"E48.MirrorCS")])]});
            var Q2;
            Q2=makeQuery(id+"F19.opExtrude","SWEPT_EDGE",EDGE,{"disambiguationData":[OSD([sQuery(id+"F18.wireOp",EDGE,"E45.MirrorCS"),sQuery(id+"F18.wireOp",EDGE,"E50.MirrorCS")])]});
            var Q3;
            Q3=makeQuery(id+"F19.opExtrude","SWEPT_EDGE",EDGE,{"disambiguationData":[OSD([sQuery(id+"F4.wireOp",EDGE,"E9"),sQuery(id+"F4.wireOp",EDGE,"E10"),sQuery(id+"F18.wireOp",EDGE,"E46.MirrorCS"),sQuery(id+"F18.wireOp",EDGE,"E50.MirrorCS")])]});
            var Q4;
            Q4=makeQuery(id+"F19.opExtrude","SWEPT_EDGE",EDGE,{"disambiguationData":[OSD([sQuery(id+"F18.wireOp",EDGE,"E34.MirrorCS"),sQuery(id+"F18.wireOp",EDGE,"E35.MirrorCS")])]});
            var Q5;
            Q5=makeQuery(id+"F19.opExtrude","SWEPT_EDGE",EDGE,{"disambiguationData":[OSD([sQuery(id+"F18.wireOp",EDGE,"E33.MirrorCS"),sQuery(id+"F18.wireOp",EDGE,"E35.MirrorCS")])]});
            var Q6;
            Q6=makeQuery(id+"F19.opExtrude","SWEPT_EDGE",EDGE,{"disambiguationData":[OSD([sQuery(id+"F18.wireOp",EDGE,"E34.MirrorCS"),sQuery(id+"F18.wireOp",EDGE,"E40.MirrorCS")])]});
            var Q7;
            Q7=makeQuery(id+"F19.opExtrude","SWEPT_EDGE",EDGE,{"disambiguationData":[OSD([sQuery(id+"F18.wireOp",EDGE,"E38.MirrorCS"),sQuery(id+"F18.wireOp",EDGE,"E55.MirrorCS")])]});
            var Q8;
            Q8=makeQuery(id+"F19.opExtrude","SWEPT_EDGE",EDGE,{"disambiguationData":[OSD([sQuery(id+"F18.wireOp",EDGE,"E38.MirrorCS"),sQuery(id+"F18.wireOp",EDGE,"E39.MirrorCS")])]});
            var Q9;
            Q9=makeQuery(id+"F19.opExtrude","SWEPT_EDGE",EDGE,{"disambiguationData":[OSD([sQuery(id+"F18.wireOp",EDGE,"E39.MirrorCS"),sQuery(id+"F18.wireOp",EDGE,"E54.MirrorCS")])]});
            var Q10;
            Q10=makeQuery(id+"F19.opExtrude","SWEPT_EDGE",EDGE,{"disambiguationData":[OSD([sQuery(id+"F18.wireOp",EDGE,"E54.MirrorCS"),sQuery(id+"F18.wireOp",EDGE,"E55.MirrorCS")])]});
            var Q11;
            Q11=makeQuery(id+"F19.opExtrude","SWEPT_EDGE",EDGE,{"disambiguationData":[OSD([sQuery(id+"F18.wireOp",EDGE,"E33.MirrorCS"),sQuery(id+"F18.wireOp",EDGE,"E40.MirrorCS")])]});
            var Q12;
            Q12=makeQuery(id+"F19.opExtrude","SWEPT_EDGE",EDGE,{"disambiguationData":[OSD([sQuery(id+"F4.wireOp",EDGE,"E10"),sQuery(id+"F18.wireOp",EDGE,"E41.MirrorCS"),sQuery(id+"F18.wireOp",EDGE,"E44.MirrorCS")])]});
            var Q13;
            Q13=makeQuery(id+"F19.opExtrude","SWEPT_EDGE",EDGE,{"disambiguationData":[OSD([sQuery(id+"F4.wireOp",EDGE,"E10"),sQuery(id+"F18.wireOp",EDGE,"E42.MirrorCS"),sQuery(id+"F18.wireOp",EDGE,"E44.MirrorCS")])]});
            var Q14;
            Q14=makeQuery(id+"F19.opExtrude","SWEPT_EDGE",EDGE,{"disambiguationData":[OSD([sQuery(id+"F4.wireOp",EDGE,"E8"),sQuery(id+"F18.wireOp",EDGE,"E42.MirrorCS"),sQuery(id+"F18.wireOp",EDGE,"E43.MirrorCS")])]});
            var Q15;
            Q15=makeQuery(id+"F19.opExtrude","SWEPT_EDGE",EDGE,{"disambiguationData":[OSD([sQuery(id+"F18.wireOp",EDGE,"E47.MirrorCS"),sQuery(id+"F18.wireOp",EDGE,"E51.MirrorCS")])]});
            var Q16;
            Q16=makeQuery(id+"F19.opExtrude","SWEPT_EDGE",EDGE,{"disambiguationData":[OSD([sQuery(id+"F18.wireOp",EDGE,"E49.MirrorCS"),sQuery(id+"F18.wireOp",EDGE,"E51.MirrorCS")])]});
            var Q17;
            Q17=makeQuery(id+"F19.opExtrude","SWEPT_EDGE",EDGE,{"disambiguationData":[OSD([sQuery(id+"F18.wireOp",EDGE,"E32.MirrorCS"),sQuery(id+"F18.wireOp",EDGE,"E49.MirrorCS")])]});
            var Q18;
            Q18=makeQuery(id+"F19.opExtrude","SWEPT_EDGE",EDGE,{"disambiguationData":[OSD([sQuery(id+"F18.wireOp",EDGE,"E36.MirrorCS"),sQuery(id+"F18.wireOp",EDGE,"E53.MirrorCS")])]});
            var Q19;
            Q19=makeQuery(id+"F19.opExtrude","SWEPT_EDGE",EDGE,{"disambiguationData":[OSD([sQuery(id+"F18.wireOp",EDGE,"E52.MirrorCS"),sQuery(id+"F18.wireOp",EDGE,"E53.MirrorCS")])]});
            var Q20;
            Q20=makeQuery(id+"F19.opExtrude","SWEPT_EDGE",EDGE,{"disambiguationData":[OSD([sQuery(id+"F18.wireOp",EDGE,"E37.MirrorCS"),sQuery(id+"F18.wireOp",EDGE,"E52.MirrorCS")])]});
            var Q21;
            Q21=makeQuery(id+"F19.opExtrude","SWEPT_EDGE",EDGE,{"disambiguationData":[OSD([sQuery(id+"F18.wireOp",EDGE,"E31.top"),sQuery(id+"F18.wireOp",EDGE,"E31.right")])]});
            var Q22;
            Q22=makeQuery(id+"F19.opExtrude","SWEPT_EDGE",EDGE,{"disambiguationData":[OSD([sQuery(id+"F18.wireOp",EDGE,"E31.top"),sQuery(id+"F18.wireOp",EDGE,"E31.left")])]});
            var Q23;
            Q23=makeQuery(id+"F19.opExtrude","SWEPT_EDGE",EDGE,{"disambiguationData":[OSD([sQuery(id+"F18.wireOp",EDGE,"E31.bottom"),sQuery(id+"F18.wireOp",EDGE,"E31.left")])]});
            var Q24;
            Q24=makeQuery(id+"F19.opExtrude","SWEPT_EDGE",EDGE,{"disambiguationData":[OSD([sQuery(id+"F18.wireOp",EDGE,"E30.bottom"),sQuery(id+"F18.wireOp",EDGE,"E30.right")])]});
            var Q25;
            Q25=makeQuery(id+"F19.opExtrude","SWEPT_EDGE",EDGE,{"disambiguationData":[OSD([sQuery(id+"F18.wireOp",EDGE,"E30.bottom"),sQuery(id+"F18.wireOp",EDGE,"E30.left")])]});
            var Q26;
            Q26=makeQuery(id+"F19.opExtrude","SWEPT_EDGE",EDGE,{"disambiguationData":[OSD([sQuery(id+"F18.wireOp",EDGE,"E30.top"),sQuery(id+"F18.wireOp",EDGE,"E30.left")])]});
            fillet(context, id + "F60", {"entities" : qUnion([Q0, Q1, Q2, Q3, Q4, Q5, Q6, Q7, Q8, Q9, Q10, Q11, Q12, Q13, Q14, Q15, Q16, Q17, Q18, Q19, Q20, Q21, Q22, Q23, Q24, Q25, Q26]), "radius" : 3 * mm, "tangentPropagation" : true, "allowEdgeOverflow" : false});
        }
        {
            var Q0;
            Q0=makeQuery(id+"F21.opExtrude","CAP_EDGE",EDGE,{"disambiguationData":[OSD([sQuery(id+"F20.wireOp",EDGE,"E58.bottom")])],"isStart":false});
            var Q1;
            Q1=makeQuery(id+"F21.opExtrude","CAP_EDGE",EDGE,{"disambiguationData":[OSD([sQuery(id+"F20.wireOp",EDGE,"E58.bottom")])],"isStart":true});
            var Q2;
            Q2=makeQuery(id+"F21.opExtrude","CAP_EDGE",EDGE,{"disambiguationData":[OSD([sQuery(id+"F20.wireOp",EDGE,"E58.top")])],"isStart":true});
            var Q3;
            Q3=makeQuery(id+"F21.opExtrude","CAP_EDGE",EDGE,{"disambiguationData":[OSD([sQuery(id+"F20.wireOp",EDGE,"E58.top")])],"isStart":false});
            var Q4;
            Q4=makeQuery(id+"F17.opExtrude","SWEPT_EDGE",EDGE,{"disambiguationData":[OSD([sQuery(id+"F0.wireOp",EDGE,"E2"),sQuery(id+"F8.wireOp",EDGE,"E22.top"),sQuery(id+"F8.wireOp",EDGE,"E22.right"),sQuery(id+"F16.wireOp",EDGE,"E25.top"),sQuery(id+"F16.wireOp",EDGE,"E25.left")])]});
            var Q5;
            Q5=makeQuery(id+"F17.opExtrude","SWEPT_EDGE",EDGE,{"disambiguationData":[OSD([sQuery(id+"F0.wireOp",EDGE,"E2"),sQuery(id+"F8.wireOp",EDGE,"E22.bottom"),sQuery(id+"F8.wireOp",EDGE,"E22.right"),sQuery(id+"F16.wireOp",EDGE,"E25.bottom"),sQuery(id+"F16.wireOp",EDGE,"E25.left")])]});
            var Q6;
            Q6=makeQuery(id+"F17.opExtrude","SWEPT_EDGE",EDGE,{"disambiguationData":[OSD([sQuery(id+"F0.wireOp",EDGE,"E2"),sQuery(id+"F8.wireOp",EDGE,"E22.top"),sQuery(id+"F8.wireOp",EDGE,"E22.right"),sQuery(id+"F16.wireOp",EDGE,"E25.top"),sQuery(id+"F16.wireOp",EDGE,"E25.right")])]});
            var Q7;
            Q7=makeQuery(id+"F23.opExtrude","CAP_EDGE",EDGE,{"disambiguationData":[OSD([sQuery(id+"F22.wireOp",EDGE,"E61.bottom")])],"isStart":true});
            var Q8;
            Q8=makeQuery(id+"F23.opExtrude","CAP_EDGE",EDGE,{"disambiguationData":[OSD([sQuery(id+"F22.wireOp",EDGE,"E61.top")])],"isStart":true});
            var Q9;
            Q9=makeQuery(id+"F23.opExtrude","CAP_EDGE",EDGE,{"disambiguationData":[OSD([sQuery(id+"F22.wireOp",EDGE,"E61.top")])],"isStart":false});
            var Q10;
            Q10=makeQuery(id+"F1.opExtrude","CAP_EDGE",EDGE,{"disambiguationData":[OSD([sQuery(id+"F0.wireOp",EDGE,"E2")])],"isStart":false});
            var Q11;
            Q11=makeQuery(id+"F1.opExtrude","CAP_EDGE",EDGE,{"disambiguationData":[OSD([sQuery(id+"F0.wireOp",EDGE,"E2")])],"isStart":true});
            var Q12;
            Q12=makeQuery(id+"F1.opExtrude","CAP_EDGE",EDGE,{"disambiguationData":[OSD([sQuery(id+"F0.wireOp",EDGE,"E0")])],"isStart":true});
            var Q13;
            Q13=makeQuery(id+"F25.opExtrude","CAP_EDGE",EDGE,{"disambiguationData":[OSD([sQuery(id+"F24.wireOp",EDGE,"E62.top")])],"isStart":false});
            var Q14;
            Q14=makeQuery(id+"F25.opExtrude","CAP_EDGE",EDGE,{"disambiguationData":[OSD([sQuery(id+"F24.wireOp",EDGE,"E62.bottom")])],"isStart":false});
            var Q15;
            Q15=makeQuery(id+"F25.opExtrude","CAP_EDGE",EDGE,{"disambiguationData":[OSD([sQuery(id+"F24.wireOp",EDGE,"E62.bottom")])],"isStart":true});
            var Q16;
            Q16=makeQuery(id+"F25.opExtrude","CAP_EDGE",EDGE,{"disambiguationData":[OSD([sQuery(id+"F24.wireOp",EDGE,"E63.top")])],"isStart":false});
            var Q17;
            Q17=makeQuery(id+"F25.opExtrude","CAP_EDGE",EDGE,{"disambiguationData":[OSD([sQuery(id+"F24.wireOp",EDGE,"E63.bottom")])],"isStart":false});
            var Q18;
            Q18=makeQuery(id+"F25.opExtrude","CAP_EDGE",EDGE,{"disambiguationData":[OSD([sQuery(id+"F24.wireOp",EDGE,"E64.bottom")])],"isStart":true});
            var Q19;
            Q19=makeQuery(id+"F25.opExtrude","CAP_EDGE",EDGE,{"disambiguationData":[OSD([sQuery(id+"F24.wireOp",EDGE,"E64.bottom")])],"isStart":false});
            var Q20;
            Q20=makeQuery(id+"F25.opExtrude","CAP_EDGE",EDGE,{"disambiguationData":[OSD([sQuery(id+"F24.wireOp",EDGE,"E64.top")])],"isStart":false});
            var Q21;
            Q21=makeQuery(id+"F23.opExtrude","CAP_EDGE",EDGE,{"disambiguationData":[OSD([sQuery(id+"F22.wireOp",EDGE,"E59.bottom")])],"isStart":true});
            var Q22;
            Q22=makeQuery(id+"F23.opExtrude","CAP_EDGE",EDGE,{"disambiguationData":[OSD([sQuery(id+"F22.wireOp",EDGE,"E59.top")])],"isStart":true});
            var Q23;
            Q23=makeQuery(id+"F23.opExtrude","CAP_EDGE",EDGE,{"disambiguationData":[OSD([sQuery(id+"F22.wireOp",EDGE,"E59.top")])],"isStart":false});
            var Q24;
            Q24=makeQuery(id+"F11.opExtrude","SWEPT_EDGE",EDGE,{"disambiguationData":[OSD([sQuery(id+"F2.wireOp",EDGE,"E4"),sQuery(id+"F10.wireOp",EDGE,"E23.bottom"),sQuery(id+"F10.wireOp",EDGE,"E23.left")])]});
            var Q25;
            Q25=makeQuery(id+"F11.opExtrude","SWEPT_EDGE",EDGE,{"disambiguationData":[OSD([sQuery(id+"F2.wireOp",EDGE,"E4"),sQuery(id+"F10.wireOp",EDGE,"E23.top"),sQuery(id+"F10.wireOp",EDGE,"E23.left")])]});
            var Q26;
            Q26=makeQuery(id+"F11.opExtrude","SWEPT_EDGE",EDGE,{"disambiguationData":[OSD([sQuery(id+"F2.wireOp",EDGE,"E4"),sQuery(id+"F10.wireOp",EDGE,"E23.top"),sQuery(id+"F10.wireOp",EDGE,"E23.right")])]});
            var Q27;
            Q27=makeQuery(id+"F21.opExtrude","CAP_EDGE",EDGE,{"disambiguationData":[OSD([sQuery(id+"F20.wireOp",EDGE,"E56.bottom")])],"isStart":true});
            var Q28;
            Q28=makeQuery(id+"F21.opExtrude","CAP_EDGE",EDGE,{"disambiguationData":[OSD([sQuery(id+"F20.wireOp",EDGE,"E56.top")])],"isStart":true});
            var Q29;
            Q29=makeQuery(id+"F21.opExtrude","CAP_EDGE",EDGE,{"disambiguationData":[OSD([sQuery(id+"F20.wireOp",EDGE,"E56.top")])],"isStart":false});
            var Q30;
            Q30=makeQuery(id+"F23.opExtrude","CAP_EDGE",EDGE,{"disambiguationData":[OSD([sQuery(id+"F22.wireOp",EDGE,"E60.top")])],"isStart":false});
            var Q31;
            Q31=makeQuery(id+"F23.opExtrude","CAP_EDGE",EDGE,{"disambiguationData":[OSD([sQuery(id+"F22.wireOp",EDGE,"E60.top")])],"isStart":true});
            var Q32;
            Q32=makeQuery(id+"F23.opExtrude","CAP_EDGE",EDGE,{"disambiguationData":[OSD([sQuery(id+"F22.wireOp",EDGE,"E60.bottom")])],"isStart":true});
            var Q33;
            Q33=makeQuery(id+"F14.opExtrude","SWEPT_EDGE",EDGE,{"disambiguationData":[OSD([sQuery(id+"F0.wireOp",EDGE,"E2"),sQuery(id+"F8.wireOp",EDGE,"E21.top"),sQuery(id+"F8.wireOp",EDGE,"E21.right"),sQuery(id+"F13.wireOp",EDGE,"E24.top"),sQuery(id+"F13.wireOp",EDGE,"E24.right")])]});
            var Q34;
            Q34=makeQuery(id+"F14.opExtrude","SWEPT_EDGE",EDGE,{"disambiguationData":[OSD([sQuery(id+"F0.wireOp",EDGE,"E2"),sQuery(id+"F8.wireOp",EDGE,"E21.top"),sQuery(id+"F8.wireOp",EDGE,"E21.right"),sQuery(id+"F13.wireOp",EDGE,"E24.top"),sQuery(id+"F13.wireOp",EDGE,"E24.left")])]});
            var Q35;
            Q35=makeQuery(id+"F14.opExtrude","SWEPT_EDGE",EDGE,{"disambiguationData":[OSD([sQuery(id+"F0.wireOp",EDGE,"E2"),sQuery(id+"F8.wireOp",EDGE,"E21.bottom"),sQuery(id+"F8.wireOp",EDGE,"E21.right"),sQuery(id+"F13.wireOp",EDGE,"E24.bottom"),sQuery(id+"F13.wireOp",EDGE,"E24.left")])]});
            var Q36;
            Q36=makeQuery(id+"F11.opExtrude","SWEPT_EDGE",EDGE,{"disambiguationData":[OSD([sQuery(id+"F2.wireOp",EDGE,"E4"),sQuery(id+"F10.wireOp",EDGE,"E23.bottom"),sQuery(id+"F10.wireOp",EDGE,"E23.right")])]});
            var Q37;
            Q37=makeQuery(id+"F14.opExtrude","SWEPT_EDGE",EDGE,{"disambiguationData":[OSD([sQuery(id+"F0.wireOp",EDGE,"E2"),sQuery(id+"F8.wireOp",EDGE,"E21.bottom"),sQuery(id+"F8.wireOp",EDGE,"E21.right"),sQuery(id+"F13.wireOp",EDGE,"E24.bottom"),sQuery(id+"F13.wireOp",EDGE,"E24.right")])]});
            var Q38;
            Q38=makeQuery(id+"F23.opExtrude","CAP_EDGE",EDGE,{"disambiguationData":[OSD([sQuery(id+"F22.wireOp",EDGE,"E60.bottom")])],"isStart":false});
            var Q39;
            Q39=makeQuery(id+"F23.opExtrude","CAP_EDGE",EDGE,{"disambiguationData":[OSD([sQuery(id+"F22.wireOp",EDGE,"E59.bottom")])],"isStart":false});
            var Q40;
            Q40=makeQuery(id+"F23.opExtrude","CAP_EDGE",EDGE,{"disambiguationData":[OSD([sQuery(id+"F22.wireOp",EDGE,"E61.bottom")])],"isStart":false});
            var Q41;
            Q41=makeQuery(id+"F25.opExtrude","CAP_EDGE",EDGE,{"disambiguationData":[OSD([sQuery(id+"F24.wireOp",EDGE,"E62.top")])],"isStart":true});
            var Q42;
            Q42=makeQuery(id+"F25.opExtrude","CAP_EDGE",EDGE,{"disambiguationData":[OSD([sQuery(id+"F24.wireOp",EDGE,"E63.top")])],"isStart":true});
            var Q43;
            Q43=makeQuery(id+"F31.opExtrude","CAP_EDGE",EDGE,{"disambiguationData":[OSD([sQuery(id+"F30.wireOp",EDGE,"E70.bottom")])],"isStart":false});
            var Q44;
            Q44=makeQuery(id+"F31.opExtrude","CAP_EDGE",EDGE,{"disambiguationData":[OSD([sQuery(id+"F30.wireOp",EDGE,"E70.bottom")])],"isStart":true});
            var Q45;
            Q45=makeQuery(id+"F31.opExtrude","CAP_EDGE",EDGE,{"disambiguationData":[OSD([sQuery(id+"F30.wireOp",EDGE,"E69.bottom")])],"isStart":false});
            var Q46;
            Q46=makeQuery(id+"F31.opExtrude","CAP_EDGE",EDGE,{"disambiguationData":[OSD([sQuery(id+"F30.wireOp",EDGE,"E69.bottom")])],"isStart":true});
            var Q47;
            Q47=makeQuery(id+"F31.opExtrude","CAP_EDGE",EDGE,{"disambiguationData":[OSD([sQuery(id+"F30.wireOp",EDGE,"E69.top")])],"isStart":true});
            var Q48;
            Q48=makeQuery(id+"F31.opExtrude","CAP_EDGE",EDGE,{"disambiguationData":[OSD([sQuery(id+"F30.wireOp",EDGE,"E70.top")])],"isStart":true});
            var Q49;
            Q49=makeQuery(id+"F29.opExtrude","CAP_EDGE",EDGE,{"disambiguationData":[OSD([sQuery(id+"F28.wireOp",EDGE,"E67.bottom")])],"isStart":false});
            var Q50;
            Q50=makeQuery(id+"F29.opExtrude","CAP_EDGE",EDGE,{"disambiguationData":[OSD([sQuery(id+"F28.wireOp",EDGE,"E67.bottom")])],"isStart":true});
            var Q51;
            Q51=makeQuery(id+"F29.opExtrude","CAP_EDGE",EDGE,{"disambiguationData":[OSD([sQuery(id+"F28.wireOp",EDGE,"E67.top")])],"isStart":true});
            var Q52;
            Q52=makeQuery(id+"F29.opExtrude","CAP_EDGE",EDGE,{"disambiguationData":[OSD([sQuery(id+"F28.wireOp",EDGE,"E68.bottom")])],"isStart":true});
            var Q53;
            Q53=makeQuery(id+"F29.opExtrude","CAP_EDGE",EDGE,{"disambiguationData":[OSD([sQuery(id+"F28.wireOp",EDGE,"E68.top")])],"isStart":true});
            var Q54;
            Q54=makeQuery(id+"F29.opExtrude","CAP_EDGE",EDGE,{"disambiguationData":[OSD([sQuery(id+"F28.wireOp",EDGE,"E68.bottom")])],"isStart":false});
            var Q55;
            Q55=makeQuery(id+"F21.opExtrude","CAP_EDGE",EDGE,{"disambiguationData":[OSD([sQuery(id+"F20.wireOp",EDGE,"E57.bottom")])],"isStart":false});
            var Q56;
            Q56=makeQuery(id+"F21.opExtrude","CAP_EDGE",EDGE,{"disambiguationData":[OSD([sQuery(id+"F20.wireOp",EDGE,"E57.bottom")])],"isStart":true});
            var Q57;
            Q57=makeQuery(id+"F21.opExtrude","CAP_EDGE",EDGE,{"disambiguationData":[OSD([sQuery(id+"F20.wireOp",EDGE,"E57.top")])],"isStart":true});
            var Q58;
            Q58=makeQuery(id+"F21.opExtrude","CAP_EDGE",EDGE,{"disambiguationData":[OSD([sQuery(id+"F20.wireOp",EDGE,"E56.bottom")])],"isStart":false});
            var Q59;
            Q59=makeQuery(id+"F33.opExtrude","CAP_EDGE",EDGE,{"disambiguationData":[OSD([sQuery(id+"F32.wireOp",EDGE,"E71.bottom")])],"isStart":true});
            var Q60;
            Q60=makeQuery(id+"F33.opExtrude","CAP_EDGE",EDGE,{"disambiguationData":[OSD([sQuery(id+"F32.wireOp",EDGE,"E71.bottom")])],"isStart":false});
            var Q61;
            Q61=makeQuery(id+"F33.opExtrude","CAP_EDGE",EDGE,{"disambiguationData":[OSD([sQuery(id+"F32.wireOp",EDGE,"E71.top")])],"isStart":false});
            var Q62;
            Q62=makeQuery(id+"F33.opExtrude","CAP_EDGE",EDGE,{"disambiguationData":[OSD([sQuery(id+"F32.wireOp",EDGE,"E72.top")])],"isStart":false});
            var Q63;
            Q63=makeQuery(id+"F33.opExtrude","CAP_EDGE",EDGE,{"disambiguationData":[OSD([sQuery(id+"F32.wireOp",EDGE,"E72.bottom")])],"isStart":false});
            var Q64;
            Q64=makeQuery(id+"F33.opExtrude","CAP_EDGE",EDGE,{"disambiguationData":[OSD([sQuery(id+"F32.wireOp",EDGE,"E72.bottom")])],"isStart":true});
            var Q65;
            Q65=makeQuery(id+"F9.opExtrude","SWEPT_EDGE",EDGE,{"disambiguationData":[OSD([sQuery(id+"F0.wireOp",EDGE,"E2"),sQuery(id+"F8.wireOp",EDGE,"E21.bottom"),sQuery(id+"F8.wireOp",EDGE,"E21.left")])]});
            var Q66;
            Q66=makeQuery(id+"F9.opExtrude","SWEPT_EDGE",EDGE,{"disambiguationData":[OSD([sQuery(id+"F0.wireOp",EDGE,"E2"),sQuery(id+"F8.wireOp",EDGE,"E21.bottom"),sQuery(id+"F8.wireOp",EDGE,"E21.right")])]});
            var Q67;
            Q67=makeQuery(id+"F9.opExtrude","SWEPT_EDGE",EDGE,{"disambiguationData":[OSD([sQuery(id+"F0.wireOp",EDGE,"E2"),sQuery(id+"F8.wireOp",EDGE,"E21.top"),sQuery(id+"F8.wireOp",EDGE,"E21.right")])]});
            var Q68;
            Q68=makeQuery(id+"F9.opExtrude","SWEPT_EDGE",EDGE,{"disambiguationData":[OSD([sQuery(id+"F0.wireOp",EDGE,"E2"),sQuery(id+"F8.wireOp",EDGE,"E22.bottom"),sQuery(id+"F8.wireOp",EDGE,"E22.left")])]});
            var Q69;
            Q69=makeQuery(id+"F9.opExtrude","SWEPT_EDGE",EDGE,{"disambiguationData":[OSD([sQuery(id+"F0.wireOp",EDGE,"E2"),sQuery(id+"F8.wireOp",EDGE,"E22.bottom"),sQuery(id+"F8.wireOp",EDGE,"E22.right")])]});
            var Q70;
            Q70=makeQuery(id+"F9.opExtrude","SWEPT_EDGE",EDGE,{"disambiguationData":[OSD([sQuery(id+"F0.wireOp",EDGE,"E2"),sQuery(id+"F8.wireOp",EDGE,"E22.top"),sQuery(id+"F8.wireOp",EDGE,"E22.right")])]});
            var Q71;
            Q71=makeQuery(id+"F27.opExtrude","CAP_EDGE",EDGE,{"disambiguationData":[OSD([sQuery(id+"F26.wireOp",EDGE,"E65.bottom")])],"isStart":false});
            var Q72;
            Q72=makeQuery(id+"F27.opExtrude","CAP_EDGE",EDGE,{"disambiguationData":[OSD([sQuery(id+"F26.wireOp",EDGE,"E65.bottom")])],"isStart":true});
            var Q73;
            Q73=makeQuery(id+"F27.opExtrude","CAP_EDGE",EDGE,{"disambiguationData":[OSD([sQuery(id+"F26.wireOp",EDGE,"E65.top")])],"isStart":true});
            var Q74;
            Q74=makeQuery(id+"F27.opExtrude","CAP_EDGE",EDGE,{"disambiguationData":[OSD([sQuery(id+"F26.wireOp",EDGE,"E66.bottom")])],"isStart":false});
            var Q75;
            Q75=makeQuery(id+"F27.opExtrude","CAP_EDGE",EDGE,{"disambiguationData":[OSD([sQuery(id+"F26.wireOp",EDGE,"E66.top")])],"isStart":true});
            var Q76;
            Q76=makeQuery(id+"F27.opExtrude","CAP_EDGE",EDGE,{"disambiguationData":[OSD([sQuery(id+"F26.wireOp",EDGE,"E66.bottom")])],"isStart":true});
            fillet(context, id + "F61", {"entities" : qUnion([Q0, Q1, Q2, Q3, Q4, Q5, Q6, Q7, Q8, Q9, Q10, Q11, Q12, Q13, Q14, Q15, Q16, Q17, Q18, Q19, Q20, Q21, Q22, Q23, Q24, Q25, Q26, Q27, Q28, Q29, Q30, Q31, Q32, Q33, Q34, Q35, Q36, Q37, Q38, Q39, Q40, Q41, Q42, Q43, Q44, Q45, Q46, Q47, Q48, Q49, Q50, Q51, Q52, Q53, Q54, Q55, Q56, Q57, Q58, Q59, Q60, Q61, Q62, Q63, Q64, Q65, Q66, Q67, Q68, Q69, Q70, Q71, Q72, Q73, Q74, Q75, Q76]), "radius" : 3 * mm, "tangentPropagation" : true, "allowEdgeOverflow" : false});
        }
        {
            var Q0;
            Q0=makeQuery(id+"F27.opExtrude","CAP_EDGE",EDGE,{"disambiguationData":[OSD([sQuery(id+"F26.wireOp",EDGE,"E65.top")])],"isStart":false});
            var Q1;
            Q1=makeQuery(id+"F7.opExtrude","CAP_EDGE",EDGE,{"disambiguationData":[OSD([sQuery(id+"F6.wireOp",EDGE,"E14")])],"isStart":true});
            var Q2;
            Q2=makeQuery(id+"F29.opExtrude","CAP_EDGE",EDGE,{"disambiguationData":[OSD([sQuery(id+"F28.wireOp",EDGE,"E67.top")])],"isStart":false});
            var Q3;
            Q3=makeQuery(id+"F29.opExtrude","CAP_EDGE",EDGE,{"disambiguationData":[OSD([sQuery(id+"F28.wireOp",EDGE,"E68.top")])],"isStart":false});
            var Q4;
            Q4=makeQuery(id+"F27.opExtrude","CAP_EDGE",EDGE,{"disambiguationData":[OSD([sQuery(id+"F26.wireOp",EDGE,"E66.top")])],"isStart":false});
            var Q5;
            Q5=makeQuery(id+"F25.opExtrude","CAP_EDGE",EDGE,{"disambiguationData":[OSD([sQuery(id+"F24.wireOp",EDGE,"E63.bottom")])],"isStart":true});
            var Q6;
            Q6=makeQuery(id+"F21.opExtrude","CAP_EDGE",EDGE,{"disambiguationData":[OSD([sQuery(id+"F20.wireOp",EDGE,"E57.top")])],"isStart":false});
            var Q7;
            Q7=makeQuery(id+"F33.opExtrude","CAP_EDGE",EDGE,{"disambiguationData":[OSD([sQuery(id+"F32.wireOp",EDGE,"E72.top")])],"isStart":true});
            var Q8;
            Q8=makeQuery(id+"F3.opExtrude","CAP_EDGE",EDGE,{"disambiguationData":[OSD([sQuery(id+"F2.wireOp",EDGE,"E6")])],"isStart":true});
            var Q9;
            Q9=makeQuery(id+"F3.opExtrude","CAP_EDGE",EDGE,{"disambiguationData":[OSD([sQuery(id+"F2.wireOp",EDGE,"E4")])],"isStart":true});
            var Q10;
            Q10=makeQuery(id+"F3.opExtrude","CAP_EDGE",EDGE,{"disambiguationData":[OSD([sQuery(id+"F2.wireOp",EDGE,"E4")])],"isStart":false});
            var Q11;
            Q11=makeQuery(id+"F3.opExtrude","CAP_EDGE",EDGE,{"disambiguationData":[OSD([sQuery(id+"F2.wireOp",EDGE,"E6")])],"isStart":false});
            var Q12;
            Q12=makeQuery(id+"F19.opExtrude","SWEPT_EDGE",EDGE,{"disambiguationData":[OSD([sQuery(id+"F4.wireOp",EDGE,"E10"),sQuery(id+"F18.wireOp",EDGE,"E27.bottom"),sQuery(id+"F18.wireOp",EDGE,"E27.left")])]});
            var Q13;
            Q13=makeQuery(id+"F5.opExtrude","CAP_EDGE",EDGE,{"disambiguationData":[OSD([sQuery(id+"F4.wireOp",EDGE,"E10")])],"isStart":false});
            var Q14;
            Q14=makeQuery(id+"F5.opExtrude","CAP_EDGE",EDGE,{"disambiguationData":[OSD([sQuery(id+"F4.wireOp",EDGE,"E8")])],"isStart":false});
            var Q15;
            Q15=makeQuery(id+"F19.opExtrude","SWEPT_EDGE",EDGE,{"disambiguationData":[OSD([sQuery(id+"F4.wireOp",EDGE,"E8"),sQuery(id+"F18.wireOp",EDGE,"E27.top"),sQuery(id+"F18.wireOp",EDGE,"E27.left")])]});
            var Q16;
            Q16=makeQuery(id+"F19.opExtrude","SWEPT_EDGE",EDGE,{"disambiguationData":[OSD([sQuery(id+"F18.wireOp",EDGE,"E29.bottom"),sQuery(id+"F18.wireOp",EDGE,"E29.left")])]});
            var Q17;
            Q17=makeQuery(id+"F5.opExtrude","CAP_EDGE",EDGE,{"disambiguationData":[OSD([sQuery(id+"F4.wireOp",EDGE,"E8")])],"isStart":true});
            var Q18;
            Q18=makeQuery(id+"F19.opExtrude","SWEPT_EDGE",EDGE,{"disambiguationData":[OSD([sQuery(id+"F4.wireOp",EDGE,"E10"),sQuery(id+"F18.wireOp",EDGE,"E27.bottom"),sQuery(id+"F18.wireOp",EDGE,"E27.right")])]});
            var Q19;
            Q19=makeQuery(id+"F19.opExtrude","SWEPT_EDGE",EDGE,{"disambiguationData":[OSD([sQuery(id+"F18.wireOp",EDGE,"E29.top"),sQuery(id+"F18.wireOp",EDGE,"E29.right")])]});
            fillet(context, id + "F62", {"entities" : qUnion([Q0, Q1, Q2, Q3, Q4, Q5, Q6, Q7, Q8, Q9, Q10, Q11, Q12, Q13, Q14, Q15, Q16, Q17, Q18, Q19]), "radius" : 3 * mm, "tangentPropagation" : true, "allowEdgeOverflow" : false});
        }
        {
            var Q0;
            Q0=makeQuery(id+"F19.opExtrude","SWEPT_EDGE",EDGE,{"disambiguationData":[OSD([sQuery(id+"F18.wireOp",EDGE,"E29.top"),sQuery(id+"F18.wireOp",EDGE,"E29.left")])]});
            var Q1;
            Q1=makeQuery(id+"F19.opExtrude","SWEPT_EDGE",EDGE,{"disambiguationData":[OSD([sQuery(id+"F18.wireOp",EDGE,"E28.top"),sQuery(id+"F18.wireOp",EDGE,"E28.right")])]});
            var Q2;
            Q2=makeQuery(id+"F19.opExtrude","SWEPT_EDGE",EDGE,{"disambiguationData":[OSD([sQuery(id+"F18.wireOp",EDGE,"E28.bottom"),sQuery(id+"F18.wireOp",EDGE,"E28.right")])]});
            var Q3;
            Q3=makeQuery(id+"F19.opExtrude","SWEPT_EDGE",EDGE,{"disambiguationData":[OSD([sQuery(id+"F18.wireOp",EDGE,"E28.top"),sQuery(id+"F18.wireOp",EDGE,"E28.left")])]});
            var Q4;
            Q4=makeQuery(id+"F19.opExtrude","SWEPT_EDGE",EDGE,{"disambiguationData":[OSD([sQuery(id+"F18.wireOp",EDGE,"E28.bottom"),sQuery(id+"F18.wireOp",EDGE,"E28.left")])]});
            var Q5;
            Q5=makeQuery(id+"F19.opExtrude","SWEPT_EDGE",EDGE,{"disambiguationData":[OSD([sQuery(id+"F18.wireOp",EDGE,"E29.bottom"),sQuery(id+"F18.wireOp",EDGE,"E29.right")])]});
            var Q6;
            Q6=makeQuery(id+"F19.opExtrude","SWEPT_EDGE",EDGE,{"disambiguationData":[OSD([sQuery(id+"F18.wireOp",EDGE,"E32.MirrorCS"),sQuery(id+"F18.wireOp",EDGE,"E47.MirrorCS")])]});
            var Q7;
            Q7=makeQuery(id+"F1.opExtrude","CAP_EDGE",EDGE,{"disambiguationData":[OSD([sQuery(id+"F0.wireOp",EDGE,"E0")])],"isStart":false});
            var Q8;
            Q8=makeQuery(id+"F17.opExtrude","SWEPT_EDGE",EDGE,{"disambiguationData":[OSD([sQuery(id+"F0.wireOp",EDGE,"E2"),sQuery(id+"F8.wireOp",EDGE,"E22.bottom"),sQuery(id+"F8.wireOp",EDGE,"E22.right"),sQuery(id+"F16.wireOp",EDGE,"E25.bottom"),sQuery(id+"F16.wireOp",EDGE,"E25.right")])]});
            var Q9;
            Q9=makeQuery(id+"F7.opExtrude","CAP_EDGE",EDGE,{"disambiguationData":[OSD([sQuery(id+"F6.wireOp",EDGE,"E12")])],"isStart":false});
            var Q10;
            Q10=makeQuery(id+"F7.opExtrude","CAP_EDGE",EDGE,{"disambiguationData":[OSD([sQuery(id+"F6.wireOp",EDGE,"E12")])],"isStart":true});
            fillet(context, id + "F63", {"entities" : qUnion([Q0, Q1, Q2, Q3, Q4, Q5, Q6, Q7, Q8, Q9, Q10]), "radius" : 3 * mm, "tangentPropagation" : true, "allowEdgeOverflow" : false});
        }
        {
            var Q0;
            Q0=makeQuery(id+"F19.opExtrude","SWEPT_EDGE",EDGE,{"disambiguationData":[OSD([sQuery(id+"F18.wireOp",EDGE,"E30.top"),sQuery(id+"F18.wireOp",EDGE,"E30.right")])]});
            var Q1;
            Q1=makeQuery(id+"F19.opExtrude","SWEPT_EDGE",EDGE,{"disambiguationData":[OSD([sQuery(id+"F4.wireOp",EDGE,"E8"),sQuery(id+"F18.wireOp",EDGE,"E26.top"),sQuery(id+"F18.wireOp",EDGE,"E26.left")])]});
            var Q2;
            Q2=makeQuery(id+"F19.opExtrude","SWEPT_EDGE",EDGE,{"disambiguationData":[OSD([sQuery(id+"F4.wireOp",EDGE,"E11"),sQuery(id+"F18.wireOp",EDGE,"E26.top"),sQuery(id+"F18.wireOp",EDGE,"E26.right")])]});
            var Q3;
            Q3=makeQuery(id+"F19.opExtrude","SWEPT_EDGE",EDGE,{"disambiguationData":[OSD([sQuery(id+"F18.wireOp",EDGE,"E26.bottom"),sQuery(id+"F18.wireOp",EDGE,"E26.right")])]});
            var Q4;
            Q4=makeQuery(id+"F19.opExtrude","SWEPT_EDGE",EDGE,{"disambiguationData":[OSD([sQuery(id+"F4.wireOp",EDGE,"E10"),sQuery(id+"F4.wireOp",EDGE,"E11"),sQuery(id+"F18.wireOp",EDGE,"E26.bottom"),sQuery(id+"F18.wireOp",EDGE,"E26.left")])]});
            fillet(context, id + "F64", {"entities" : qUnion([Q0, Q1, Q2, Q3, Q4]), "radius" : 3 * mm, "tangentPropagation" : true, "allowEdgeOverflow" : false});
        }
        {
            var Q0;
            Q0=makeQuery(id+"F19.opExtrude","SWEPT_EDGE",EDGE,{"disambiguationData":[OSD([sQuery(id+"F4.wireOp",EDGE,"E8"),sQuery(id+"F18.wireOp",EDGE,"E27.top"),sQuery(id+"F18.wireOp",EDGE,"E27.right")])]});
            var Q1;
            Q1=makeQuery(id+"F19.opExtrude","SWEPT_EDGE",EDGE,{"disambiguationData":[OSD([sQuery(id+"F18.wireOp",EDGE,"E31.bottom"),sQuery(id+"F18.wireOp",EDGE,"E31.right")])]});
            var Q2;
            Q2=makeQuery(id+"F19.opExtrude","SWEPT_EDGE",EDGE,{"disambiguationData":[OSD([sQuery(id+"F18.wireOp",EDGE,"E36.MirrorCS"),sQuery(id+"F18.wireOp",EDGE,"E37.MirrorCS")])]});
            var Q3;
            Q3=makeQuery(id+"F19.opExtrude","SWEPT_EDGE",EDGE,{"disambiguationData":[OSD([sQuery(id+"F4.wireOp",EDGE,"E8"),sQuery(id+"F18.wireOp",EDGE,"E41.MirrorCS"),sQuery(id+"F18.wireOp",EDGE,"E43.MirrorCS")])]});
            fillet(context, id + "F65", {"entities" : qUnion([Q0, Q1, Q2, Q3]), "radius" : 3 * mm, "tangentPropagation" : true, "allowEdgeOverflow" : false});
        }
        {
            var Q0;
            Q0=makeQuery(id+"F5.opExtrude","CAP_EDGE",EDGE,{"disambiguationData":[OSD([sQuery(id+"F4.wireOp",EDGE,"E10")])],"isStart":true});
            fillet(context, id + "F66", {"entities" : qUnion([Q0]), "radius" : 3 * mm, "tangentPropagation" : true, "allowEdgeOverflow" : false});
        }
        {
            var Q0;
            Q0=makeQuery(id+"F31.opExtrude","CAP_EDGE",EDGE,{"disambiguationData":[OSD([sQuery(id+"F30.wireOp",EDGE,"E69.top")])],"isStart":false});
            var Q1;
            Q1=makeQuery(id+"F33.opExtrude","CAP_EDGE",EDGE,{"disambiguationData":[OSD([sQuery(id+"F32.wireOp",EDGE,"E71.top")])],"isStart":true});
            fillet(context, id + "F67", {"entities" : qUnion([Q0, Q1]), "radius" : 3 * mm, "tangentPropagation" : true, "allowEdgeOverflow" : false});
        }
        {
            var Q0;
            Q0=makeQuery(id+"F7.opExtrude","CAP_EDGE",EDGE,{"disambiguationData":[OSD([sQuery(id+"F6.wireOp",EDGE,"E14")])],"isStart":false});
            fillet(context, id + "F68", {"entities" : qUnion([Q0]), "radius" : 3 * mm, "tangentPropagation" : true, "allowEdgeOverflow" : false});
        }
        {
            var Q0;
            Q0=makeQuery(id+"F35.boolean.opBoolean","COPY",EDGE,{"derivedFrom":makeQuery(id+"F35.opExtrude","SWEPT_EDGE",EDGE,{"disambiguationData":[OSD([sQuery(id+"F34.wireOp",EDGE,"E89.MirrorCS"),sQuery(id+"F34.wireOp",EDGE,"E101.MirrorCS")])]})});
            var Q1;
            Q1=makeQuery(id+"F35.boolean.opBoolean","COPY",EDGE,{"derivedFrom":makeQuery(id+"F35.opExtrude","SWEPT_EDGE",EDGE,{"disambiguationData":[OSD([sQuery(id+"F34.wireOp",EDGE,"E85.MirrorCS"),sQuery(id+"F34.wireOp",EDGE,"E92.MirrorCS")])]})});
            var Q2;
            Q2=makeQuery(id+"F35.boolean.opBoolean","COPY",EDGE,{"derivedFrom":makeQuery(id+"F35.opExtrude","SWEPT_EDGE",EDGE,{"disambiguationData":[OSD([sQuery(id+"F34.wireOp",EDGE,"E92.MirrorCS"),sQuery(id+"F34.wireOp",EDGE,"E101.MirrorCS")])]})});
            var Q3;
            Q3=makeQuery(id+"F35.boolean.opBoolean","COPY",EDGE,{"derivedFrom":makeQuery(id+"F35.opExtrude","SWEPT_EDGE",EDGE,{"disambiguationData":[OSD([sQuery(id+"F34.wireOp",EDGE,"E85.MirrorCS"),sQuery(id+"F34.wireOp",EDGE,"E89.MirrorCS")])]})});
            fillet(context, id + "F69", {"entities" : qUnion([Q0, Q1, Q2, Q3]), "radius" : 2 * mm, "tangentPropagation" : true, "allowEdgeOverflow" : false});
        }
        {
            var Q0;
            Q0=makeQuery(id+"F35.boolean.opBoolean","COPY",EDGE,{"derivedFrom":makeQuery(id+"F35.opExtrude","SWEPT_EDGE",EDGE,{"disambiguationData":[OSD([sQuery(id+"F34.wireOp",EDGE,"E82.MirrorCS"),sQuery(id+"F34.wireOp",EDGE,"E86.MirrorCS")])]})});
            var Q1;
            Q1=makeQuery(id+"F35.boolean.opBoolean","COPY",EDGE,{"derivedFrom":makeQuery(id+"F35.opExtrude","SWEPT_EDGE",EDGE,{"disambiguationData":[OSD([sQuery(id+"F34.wireOp",EDGE,"E81.MirrorCS"),sQuery(id+"F34.wireOp",EDGE,"E86.MirrorCS")])]})});
            var Q2;
            Q2=makeQuery(id+"F35.boolean.opBoolean","COPY",EDGE,{"derivedFrom":makeQuery(id+"F35.opExtrude","SWEPT_EDGE",EDGE,{"disambiguationData":[OSD([sQuery(id+"F34.wireOp",EDGE,"E81.MirrorCS"),sQuery(id+"F34.wireOp",EDGE,"E91.MirrorCS")])]})});
            var Q3;
            Q3=makeQuery(id+"F35.boolean.opBoolean","COPY",EDGE,{"derivedFrom":makeQuery(id+"F35.opExtrude","SWEPT_EDGE",EDGE,{"disambiguationData":[OSD([sQuery(id+"F34.wireOp",EDGE,"E82.MirrorCS"),sQuery(id+"F34.wireOp",EDGE,"E91.MirrorCS")])]})});
            fillet(context, id + "F70", {"entities" : qUnion([Q0, Q1, Q2, Q3]), "radius" : 2 * mm, "tangentPropagation" : true, "allowEdgeOverflow" : false});
        }
        {
            var Q0;
            Q0=makeQuery(id+"F35.boolean.opBoolean","COPY",EDGE,{"derivedFrom":makeQuery(id+"F35.opExtrude","SWEPT_EDGE",EDGE,{"disambiguationData":[OSD([sQuery(id+"F34.wireOp",EDGE,"E75.top"),sQuery(id+"F34.wireOp",EDGE,"E75.left")])]})});
            var Q1;
            Q1=makeQuery(id+"F35.boolean.opBoolean","COPY",EDGE,{"derivedFrom":makeQuery(id+"F35.opExtrude","SWEPT_EDGE",EDGE,{"disambiguationData":[OSD([sQuery(id+"F34.wireOp",EDGE,"E75.bottom"),sQuery(id+"F34.wireOp",EDGE,"E75.left")])]})});
            var Q2;
            Q2=makeQuery(id+"F35.boolean.opBoolean","COPY",EDGE,{"derivedFrom":makeQuery(id+"F35.opExtrude","SWEPT_EDGE",EDGE,{"disambiguationData":[OSD([sQuery(id+"F34.wireOp",EDGE,"E75.bottom"),sQuery(id+"F34.wireOp",EDGE,"E75.right")])]})});
            var Q3;
            Q3=makeQuery(id+"F35.boolean.opBoolean","COPY",EDGE,{"derivedFrom":makeQuery(id+"F35.opExtrude","SWEPT_EDGE",EDGE,{"disambiguationData":[OSD([sQuery(id+"F34.wireOp",EDGE,"E75.top"),sQuery(id+"F34.wireOp",EDGE,"E75.right")])]})});
            fillet(context, id + "F71", {"entities" : qUnion([Q0, Q1, Q2, Q3]), "radius" : 2 * mm, "tangentPropagation" : true, "allowEdgeOverflow" : false});
        }
        {
            var Q0;
            Q0=makeQuery(id+"F35.boolean.opBoolean","COPY",EDGE,{"derivedFrom":makeQuery(id+"F35.opExtrude","SWEPT_EDGE",EDGE,{"disambiguationData":[OSD([sQuery(id+"F34.wireOp",EDGE,"E73.top"),sQuery(id+"F34.wireOp",EDGE,"E73.right")])]})});
            var Q1;
            Q1=makeQuery(id+"F35.boolean.opBoolean","COPY",EDGE,{"derivedFrom":makeQuery(id+"F35.opExtrude","SWEPT_EDGE",EDGE,{"disambiguationData":[OSD([sQuery(id+"F34.wireOp",EDGE,"E73.bottom"),sQuery(id+"F34.wireOp",EDGE,"E73.right")])]})});
            var Q2;
            Q2=makeQuery(id+"F35.boolean.opBoolean","COPY",EDGE,{"derivedFrom":makeQuery(id+"F35.opExtrude","SWEPT_EDGE",EDGE,{"disambiguationData":[OSD([sQuery(id+"F34.wireOp",EDGE,"E73.top"),sQuery(id+"F34.wireOp",EDGE,"E73.left")])]})});
            var Q3;
            Q3=makeQuery(id+"F35.boolean.opBoolean","COPY",EDGE,{"derivedFrom":makeQuery(id+"F35.opExtrude","SWEPT_EDGE",EDGE,{"disambiguationData":[OSD([sQuery(id+"F34.wireOp",EDGE,"E73.bottom"),sQuery(id+"F34.wireOp",EDGE,"E73.left")])]})});
            fillet(context, id + "F72", {"entities" : qUnion([Q0, Q1, Q2, Q3]), "radius" : 2 * mm, "tangentPropagation" : true, "allowEdgeOverflow" : false});
        }
        {
            var Q0;
            Q0=makeQuery(id+"F35.boolean.opBoolean","COPY",EDGE,{"derivedFrom":makeQuery(id+"F35.opExtrude","SWEPT_EDGE",EDGE,{"disambiguationData":[OSD([sQuery(id+"F34.wireOp",EDGE,"E74.bottom"),sQuery(id+"F34.wireOp",EDGE,"E74.left")])]})});
            var Q1;
            Q1=makeQuery(id+"F35.boolean.opBoolean","COPY",EDGE,{"derivedFrom":makeQuery(id+"F35.opExtrude","SWEPT_EDGE",EDGE,{"disambiguationData":[OSD([sQuery(id+"F34.wireOp",EDGE,"E74.bottom"),sQuery(id+"F34.wireOp",EDGE,"E74.right")])]})});
            var Q2;
            Q2=makeQuery(id+"F35.boolean.opBoolean","COPY",EDGE,{"derivedFrom":makeQuery(id+"F35.opExtrude","SWEPT_EDGE",EDGE,{"disambiguationData":[OSD([sQuery(id+"F34.wireOp",EDGE,"E74.top"),sQuery(id+"F34.wireOp",EDGE,"E74.left")])]})});
            var Q3;
            Q3=makeQuery(id+"F35.boolean.opBoolean","COPY",EDGE,{"derivedFrom":makeQuery(id+"F35.opExtrude","SWEPT_EDGE",EDGE,{"disambiguationData":[OSD([sQuery(id+"F34.wireOp",EDGE,"E74.top"),sQuery(id+"F34.wireOp",EDGE,"E74.right")])]})});
            fillet(context, id + "F73", {"entities" : qUnion([Q0, Q1, Q2, Q3]), "radius" : 2 * mm, "tangentPropagation" : true, "allowEdgeOverflow" : false});
        }
        {
            var Q0;
            Q0=makeQuery(id+"F35.boolean.opBoolean","COPY",EDGE,{"derivedFrom":makeQuery(id+"F35.opExtrude","SWEPT_EDGE",EDGE,{"disambiguationData":[OSD([sQuery(id+"F34.wireOp",EDGE,"E78.top"),sQuery(id+"F34.wireOp",EDGE,"E78.right")])]})});
            var Q1;
            Q1=makeQuery(id+"F35.boolean.opBoolean","COPY",EDGE,{"derivedFrom":makeQuery(id+"F35.opExtrude","SWEPT_EDGE",EDGE,{"disambiguationData":[OSD([sQuery(id+"F34.wireOp",EDGE,"E78.top"),sQuery(id+"F34.wireOp",EDGE,"E78.left")])]})});
            var Q2;
            Q2=makeQuery(id+"F35.boolean.opBoolean","COPY",EDGE,{"derivedFrom":makeQuery(id+"F35.opExtrude","SWEPT_EDGE",EDGE,{"disambiguationData":[OSD([sQuery(id+"F34.wireOp",EDGE,"E78.bottom"),sQuery(id+"F34.wireOp",EDGE,"E78.right")])]})});
            var Q3;
            Q3=makeQuery(id+"F35.boolean.opBoolean","COPY",EDGE,{"derivedFrom":makeQuery(id+"F35.opExtrude","SWEPT_EDGE",EDGE,{"disambiguationData":[OSD([sQuery(id+"F34.wireOp",EDGE,"E78.bottom"),sQuery(id+"F34.wireOp",EDGE,"E78.left")])]})});
            fillet(context, id + "F74", {"entities" : qUnion([Q0, Q1, Q2, Q3]), "radius" : 2 * mm, "tangentPropagation" : true, "allowEdgeOverflow" : false});
        }
        {
            var Q0;
            Q0=makeQuery(id+"F35.boolean.opBoolean","COPY",EDGE,{"derivedFrom":makeQuery(id+"F35.opExtrude","SWEPT_EDGE",EDGE,{"disambiguationData":[OSD([sQuery(id+"F34.wireOp",EDGE,"E77.bottom"),sQuery(id+"F34.wireOp",EDGE,"E77.right")])]})});
            var Q1;
            Q1=makeQuery(id+"F35.boolean.opBoolean","COPY",EDGE,{"derivedFrom":makeQuery(id+"F35.opExtrude","SWEPT_EDGE",EDGE,{"disambiguationData":[OSD([sQuery(id+"F34.wireOp",EDGE,"E77.bottom"),sQuery(id+"F34.wireOp",EDGE,"E77.left")])]})});
            var Q2;
            Q2=makeQuery(id+"F35.boolean.opBoolean","COPY",EDGE,{"derivedFrom":makeQuery(id+"F35.opExtrude","SWEPT_EDGE",EDGE,{"disambiguationData":[OSD([sQuery(id+"F34.wireOp",EDGE,"E77.top"),sQuery(id+"F34.wireOp",EDGE,"E77.left")])]})});
            var Q3;
            Q3=makeQuery(id+"F35.boolean.opBoolean","COPY",EDGE,{"derivedFrom":makeQuery(id+"F35.opExtrude","SWEPT_EDGE",EDGE,{"disambiguationData":[OSD([sQuery(id+"F34.wireOp",EDGE,"E77.top"),sQuery(id+"F34.wireOp",EDGE,"E77.right")])]})});
            fillet(context, id + "F75", {"entities" : qUnion([Q0, Q1, Q2, Q3]), "radius" : 2 * mm, "tangentPropagation" : true, "allowEdgeOverflow" : false});
        }
        {
            var Q0;
            Q0=makeQuery(id+"F35.boolean.opBoolean","COPY",EDGE,{"derivedFrom":makeQuery(id+"F35.opExtrude","SWEPT_EDGE",EDGE,{"disambiguationData":[OSD([sQuery(id+"F34.wireOp",EDGE,"E83.MirrorCS"),sQuery(id+"F34.wireOp",EDGE,"E87.MirrorCS")])]})});
            var Q1;
            Q1=makeQuery(id+"F35.boolean.opBoolean","COPY",EDGE,{"derivedFrom":makeQuery(id+"F35.opExtrude","SWEPT_EDGE",EDGE,{"disambiguationData":[OSD([sQuery(id+"F34.wireOp",EDGE,"E80.MirrorCS"),sQuery(id+"F34.wireOp",EDGE,"E87.MirrorCS")])]})});
            var Q2;
            Q2=makeQuery(id+"F35.boolean.opBoolean","COPY",EDGE,{"derivedFrom":makeQuery(id+"F35.opExtrude","SWEPT_EDGE",EDGE,{"disambiguationData":[OSD([sQuery(id+"F34.wireOp",EDGE,"E79.MirrorCS"),sQuery(id+"F34.wireOp",EDGE,"E80.MirrorCS")])]})});
            var Q3;
            Q3=makeQuery(id+"F35.boolean.opBoolean","COPY",EDGE,{"derivedFrom":makeQuery(id+"F35.opExtrude","SWEPT_EDGE",EDGE,{"disambiguationData":[OSD([sQuery(id+"F34.wireOp",EDGE,"E79.MirrorCS"),sQuery(id+"F34.wireOp",EDGE,"E83.MirrorCS")])]})});
            fillet(context, id + "F76", {"entities" : qUnion([Q0, Q1, Q2, Q3]), "radius" : 2 * mm, "tangentPropagation" : true, "allowEdgeOverflow" : false});
        }
        {
            var Q0;
            Q0=makeQuery(id+"F35.boolean.opBoolean","COPY",EDGE,{"derivedFrom":makeQuery(id+"F35.opExtrude","SWEPT_EDGE",EDGE,{"disambiguationData":[OSD([sQuery(id+"F34.wireOp",EDGE,"E84.MirrorCS"),sQuery(id+"F34.wireOp",EDGE,"E94.MirrorCS")])]})});
            var Q1;
            Q1=makeQuery(id+"F35.boolean.opBoolean","COPY",EDGE,{"derivedFrom":makeQuery(id+"F35.opExtrude","SWEPT_EDGE",EDGE,{"disambiguationData":[OSD([sQuery(id+"F34.wireOp",EDGE,"E84.MirrorCS"),sQuery(id+"F34.wireOp",EDGE,"E90.MirrorCS")])]})});
            var Q2;
            Q2=makeQuery(id+"F35.boolean.opBoolean","COPY",EDGE,{"derivedFrom":makeQuery(id+"F35.opExtrude","SWEPT_EDGE",EDGE,{"disambiguationData":[OSD([sQuery(id+"F34.wireOp",EDGE,"E90.MirrorCS"),sQuery(id+"F34.wireOp",EDGE,"E98.MirrorCS")])]})});
            var Q3;
            Q3=makeQuery(id+"F35.boolean.opBoolean","COPY",EDGE,{"derivedFrom":makeQuery(id+"F35.opExtrude","SWEPT_EDGE",EDGE,{"disambiguationData":[OSD([sQuery(id+"F34.wireOp",EDGE,"E94.MirrorCS"),sQuery(id+"F34.wireOp",EDGE,"E98.MirrorCS")])]})});
            fillet(context, id + "F77", {"entities" : qUnion([Q0, Q1, Q2, Q3]), "radius" : 2 * mm, "tangentPropagation" : true, "allowEdgeOverflow" : false});
        }
        {
            var Q0;
            Q0=makeQuery(id+"F35.boolean.opBoolean","COPY",EDGE,{"derivedFrom":makeQuery(id+"F35.opExtrude","SWEPT_EDGE",EDGE,{"disambiguationData":[OSD([sQuery(id+"F34.wireOp",EDGE,"E96.MirrorCS"),sQuery(id+"F34.wireOp",EDGE,"E100.MirrorCS")])]})});
            var Q1;
            Q1=makeQuery(id+"F35.boolean.opBoolean","COPY",EDGE,{"derivedFrom":makeQuery(id+"F35.opExtrude","SWEPT_EDGE",EDGE,{"disambiguationData":[OSD([sQuery(id+"F34.wireOp",EDGE,"E96.MirrorCS"),sQuery(id+"F34.wireOp",EDGE,"E99.MirrorCS")])]})});
            var Q2;
            Q2=makeQuery(id+"F35.boolean.opBoolean","COPY",EDGE,{"derivedFrom":makeQuery(id+"F35.opExtrude","SWEPT_EDGE",EDGE,{"disambiguationData":[OSD([sQuery(id+"F34.wireOp",EDGE,"E88.MirrorCS"),sQuery(id+"F34.wireOp",EDGE,"E99.MirrorCS")])]})});
            var Q3;
            Q3=makeQuery(id+"F35.boolean.opBoolean","COPY",EDGE,{"derivedFrom":makeQuery(id+"F35.opExtrude","SWEPT_EDGE",EDGE,{"disambiguationData":[OSD([sQuery(id+"F34.wireOp",EDGE,"E88.MirrorCS"),sQuery(id+"F34.wireOp",EDGE,"E100.MirrorCS")])]})});
            fillet(context, id + "F78", {"entities" : qUnion([Q0, Q1, Q2, Q3]), "radius" : 2 * mm, "tangentPropagation" : true, "allowEdgeOverflow" : false});
        }
        {
            var Q0;
            Q0=makeQuery(id+"F35.boolean.opBoolean","COPY",EDGE,{"derivedFrom":makeQuery(id+"F35.opExtrude","SWEPT_EDGE",EDGE,{"disambiguationData":[OSD([sQuery(id+"F34.wireOp",EDGE,"E93.MirrorCS"),sQuery(id+"F34.wireOp",EDGE,"E102.MirrorCS")])]})});
            var Q1;
            Q1=makeQuery(id+"F35.boolean.opBoolean","COPY",EDGE,{"derivedFrom":makeQuery(id+"F35.opExtrude","SWEPT_EDGE",EDGE,{"disambiguationData":[OSD([sQuery(id+"F34.wireOp",EDGE,"E93.MirrorCS"),sQuery(id+"F34.wireOp",EDGE,"E97.MirrorCS")])]})});
            var Q2;
            Q2=makeQuery(id+"F35.boolean.opBoolean","COPY",EDGE,{"derivedFrom":makeQuery(id+"F35.opExtrude","SWEPT_EDGE",EDGE,{"disambiguationData":[OSD([sQuery(id+"F34.wireOp",EDGE,"E95.MirrorCS"),sQuery(id+"F34.wireOp",EDGE,"E97.MirrorCS")])]})});
            var Q3;
            Q3=makeQuery(id+"F35.boolean.opBoolean","COPY",EDGE,{"derivedFrom":makeQuery(id+"F35.opExtrude","SWEPT_EDGE",EDGE,{"disambiguationData":[OSD([sQuery(id+"F34.wireOp",EDGE,"E95.MirrorCS"),sQuery(id+"F34.wireOp",EDGE,"E102.MirrorCS")])]})});
            fillet(context, id + "F79", {"entities" : qUnion([Q0, Q1, Q2, Q3]), "radius" : 2 * mm, "tangentPropagation" : true, "allowEdgeOverflow" : false});
        }
        {
            var Q0;
            Q0=makeQuery(id+"F35.boolean.opBoolean","COPY",EDGE,{"derivedFrom":makeQuery(id+"F35.opExtrude","SWEPT_EDGE",EDGE,{"disambiguationData":[OSD([sQuery(id+"F34.wireOp",EDGE,"E76.bottom"),sQuery(id+"F34.wireOp",EDGE,"E76.left")])]})});
            var Q1;
            Q1=makeQuery(id+"F35.boolean.opBoolean","COPY",EDGE,{"derivedFrom":makeQuery(id+"F35.opExtrude","SWEPT_EDGE",EDGE,{"disambiguationData":[OSD([sQuery(id+"F34.wireOp",EDGE,"E76.bottom"),sQuery(id+"F34.wireOp",EDGE,"E76.right")])]})});
            var Q2;
            Q2=makeQuery(id+"F35.boolean.opBoolean","COPY",EDGE,{"derivedFrom":makeQuery(id+"F35.opExtrude","SWEPT_EDGE",EDGE,{"disambiguationData":[OSD([sQuery(id+"F34.wireOp",EDGE,"E76.top"),sQuery(id+"F34.wireOp",EDGE,"E76.right")])]})});
            var Q3;
            Q3=makeQuery(id+"F35.boolean.opBoolean","COPY",EDGE,{"derivedFrom":makeQuery(id+"F35.opExtrude","SWEPT_EDGE",EDGE,{"disambiguationData":[OSD([sQuery(id+"F34.wireOp",EDGE,"E76.top"),sQuery(id+"F34.wireOp",EDGE,"E76.left")])]})});
            fillet(context, id + "F80", {"entities" : qUnion([Q0, Q1, Q2, Q3]), "radius" : 2 * mm, "tangentPropagation" : true, "allowEdgeOverflow" : false});
        }
        {
            var Q0;
            Q0=makeQuery(id+"F39.boolean.opBoolean","COPY",EDGE,{"derivedFrom":makeQuery(id+"F39.opExtrude","SWEPT_EDGE",EDGE,{"disambiguationData":[OSD([sQuery(id+"F38.wireOp",EDGE,"E106.top"),sQuery(id+"F38.wireOp",EDGE,"E106.right")])]})});
            var Q1;
            Q1=makeQuery(id+"F39.boolean.opBoolean","COPY",EDGE,{"derivedFrom":makeQuery(id+"F39.opExtrude","SWEPT_EDGE",EDGE,{"disambiguationData":[OSD([sQuery(id+"F38.wireOp",EDGE,"E106.top"),sQuery(id+"F38.wireOp",EDGE,"E106.left")])]})});
            var Q2;
            Q2=makeQuery(id+"F39.boolean.opBoolean","COPY",EDGE,{"derivedFrom":makeQuery(id+"F39.opExtrude","SWEPT_EDGE",EDGE,{"disambiguationData":[OSD([sQuery(id+"F38.wireOp",EDGE,"E106.bottom"),sQuery(id+"F38.wireOp",EDGE,"E106.right")])]})});
            var Q3;
            Q3=makeQuery(id+"F39.boolean.opBoolean","COPY",EDGE,{"derivedFrom":makeQuery(id+"F39.opExtrude","SWEPT_EDGE",EDGE,{"disambiguationData":[OSD([sQuery(id+"F38.wireOp",EDGE,"E106.bottom"),sQuery(id+"F38.wireOp",EDGE,"E106.left")])]})});
            fillet(context, id + "F81", {"entities" : qUnion([Q0, Q1, Q2, Q3]), "radius" : 2 * mm, "tangentPropagation" : true, "allowEdgeOverflow" : false});
        }
        {
            var Q0;
            Q0=makeQuery(id+"F41.boolean.opBoolean","COPY",EDGE,{"derivedFrom":makeQuery(id+"F41.opExtrude","SWEPT_EDGE",EDGE,{"disambiguationData":[OSD([sQuery(id+"F40.wireOp",EDGE,"E107.top"),sQuery(id+"F40.wireOp",EDGE,"E107.right")])]})});
            var Q1;
            Q1=makeQuery(id+"F41.boolean.opBoolean","COPY",EDGE,{"derivedFrom":makeQuery(id+"F41.opExtrude","SWEPT_EDGE",EDGE,{"disambiguationData":[OSD([sQuery(id+"F40.wireOp",EDGE,"E107.bottom"),sQuery(id+"F40.wireOp",EDGE,"E107.right")])]})});
            var Q2;
            Q2=makeQuery(id+"F41.boolean.opBoolean","COPY",EDGE,{"derivedFrom":makeQuery(id+"F41.opExtrude","SWEPT_EDGE",EDGE,{"disambiguationData":[OSD([sQuery(id+"F40.wireOp",EDGE,"E107.bottom"),sQuery(id+"F40.wireOp",EDGE,"E107.left")])]})});
            var Q3;
            Q3=makeQuery(id+"F41.boolean.opBoolean","COPY",EDGE,{"derivedFrom":makeQuery(id+"F41.opExtrude","SWEPT_EDGE",EDGE,{"disambiguationData":[OSD([sQuery(id+"F40.wireOp",EDGE,"E107.top"),sQuery(id+"F40.wireOp",EDGE,"E107.left")])]})});
            fillet(context, id + "F82", {"entities" : qUnion([Q0, Q1, Q2, Q3]), "radius" : 2 * mm, "tangentPropagation" : true, "allowEdgeOverflow" : false});
        }
        {
            var Q0;
            Q0=makeQuery(id+"F49.boolean.opBoolean","COPY",EDGE,{"derivedFrom":makeQuery(id+"F49.opExtrude","SWEPT_EDGE",EDGE,{"disambiguationData":[OSD([sQuery(id+"F48.wireOp",EDGE,"E116.top"),sQuery(id+"F48.wireOp",EDGE,"E116.left")])]})});
            var Q1;
            Q1=makeQuery(id+"F49.boolean.opBoolean","COPY",EDGE,{"derivedFrom":makeQuery(id+"F49.opExtrude","SWEPT_EDGE",EDGE,{"disambiguationData":[OSD([sQuery(id+"F48.wireOp",EDGE,"E116.bottom"),sQuery(id+"F48.wireOp",EDGE,"E116.left")])]})});
            var Q2;
            Q2=makeQuery(id+"F49.boolean.opBoolean","COPY",EDGE,{"derivedFrom":makeQuery(id+"F49.opExtrude","SWEPT_EDGE",EDGE,{"disambiguationData":[OSD([sQuery(id+"F48.wireOp",EDGE,"E116.bottom"),sQuery(id+"F48.wireOp",EDGE,"E116.right")])]})});
            var Q3;
            Q3=makeQuery(id+"F49.boolean.opBoolean","COPY",EDGE,{"derivedFrom":makeQuery(id+"F49.opExtrude","SWEPT_EDGE",EDGE,{"disambiguationData":[OSD([sQuery(id+"F48.wireOp",EDGE,"E116.top"),sQuery(id+"F48.wireOp",EDGE,"E116.right")])]})});
            fillet(context, id + "F83", {"entities" : qUnion([Q0, Q1, Q2, Q3]), "radius" : 2 * mm, "tangentPropagation" : true, "allowEdgeOverflow" : false});
        }
        {
            var Q0;
            Q0=makeQuery(id+"F47.boolean.opBoolean","COPY",EDGE,{"derivedFrom":makeQuery(id+"F47.opExtrude","SWEPT_EDGE",EDGE,{"disambiguationData":[OSD([sQuery(id+"F46.wireOp",EDGE,"E113.bottom"),sQuery(id+"F46.wireOp",EDGE,"E113.right")])]})});
            var Q1;
            Q1=makeQuery(id+"F47.boolean.opBoolean","COPY",EDGE,{"derivedFrom":makeQuery(id+"F47.opExtrude","SWEPT_EDGE",EDGE,{"disambiguationData":[OSD([sQuery(id+"F46.wireOp",EDGE,"E113.bottom"),sQuery(id+"F46.wireOp",EDGE,"E113.left")])]})});
            var Q2;
            Q2=makeQuery(id+"F47.boolean.opBoolean","COPY",EDGE,{"derivedFrom":makeQuery(id+"F47.opExtrude","SWEPT_EDGE",EDGE,{"disambiguationData":[OSD([sQuery(id+"F46.wireOp",EDGE,"E113.top"),sQuery(id+"F46.wireOp",EDGE,"E113.left")])]})});
            var Q3;
            Q3=makeQuery(id+"F47.boolean.opBoolean","COPY",EDGE,{"derivedFrom":makeQuery(id+"F47.opExtrude","SWEPT_EDGE",EDGE,{"disambiguationData":[OSD([sQuery(id+"F46.wireOp",EDGE,"E113.top"),sQuery(id+"F46.wireOp",EDGE,"E113.right")])]})});
            fillet(context, id + "F84", {"entities" : qUnion([Q0, Q1, Q2, Q3]), "radius" : 2 * mm, "tangentPropagation" : true, "allowEdgeOverflow" : false});
        }
        {
            var Q0;
            Q0=makeQuery(id+"F47.boolean.opBoolean","COPY",EDGE,{"derivedFrom":makeQuery(id+"F47.opExtrude","SWEPT_EDGE",EDGE,{"disambiguationData":[OSD([sQuery(id+"F46.wireOp",EDGE,"E114.top"),sQuery(id+"F46.wireOp",EDGE,"E114.left")])]})});
            var Q1;
            Q1=makeQuery(id+"F47.boolean.opBoolean","COPY",EDGE,{"derivedFrom":makeQuery(id+"F47.opExtrude","SWEPT_EDGE",EDGE,{"disambiguationData":[OSD([sQuery(id+"F46.wireOp",EDGE,"E114.top"),sQuery(id+"F46.wireOp",EDGE,"E114.right")])]})});
            var Q2;
            Q2=makeQuery(id+"F47.boolean.opBoolean","COPY",EDGE,{"derivedFrom":makeQuery(id+"F47.opExtrude","SWEPT_EDGE",EDGE,{"disambiguationData":[OSD([sQuery(id+"F46.wireOp",EDGE,"E114.bottom"),sQuery(id+"F46.wireOp",EDGE,"E114.right")])]})});
            var Q3;
            Q3=makeQuery(id+"F47.boolean.opBoolean","COPY",EDGE,{"derivedFrom":makeQuery(id+"F47.opExtrude","SWEPT_EDGE",EDGE,{"disambiguationData":[OSD([sQuery(id+"F46.wireOp",EDGE,"E114.bottom"),sQuery(id+"F46.wireOp",EDGE,"E114.left")])]})});
            fillet(context, id + "F85", {"entities" : qUnion([Q0, Q1, Q2, Q3]), "radius" : 2 * mm, "tangentPropagation" : true, "allowEdgeOverflow" : false});
        }
        {
            var Q0;
            Q0=makeQuery(id+"F49.boolean.opBoolean","COPY",EDGE,{"derivedFrom":makeQuery(id+"F49.opExtrude","SWEPT_EDGE",EDGE,{"disambiguationData":[OSD([sQuery(id+"F48.wireOp",EDGE,"E117.top"),sQuery(id+"F48.wireOp",EDGE,"E117.right")])]})});
            var Q1;
            Q1=makeQuery(id+"F49.boolean.opBoolean","COPY",EDGE,{"derivedFrom":makeQuery(id+"F49.opExtrude","SWEPT_EDGE",EDGE,{"disambiguationData":[OSD([sQuery(id+"F48.wireOp",EDGE,"E117.bottom"),sQuery(id+"F48.wireOp",EDGE,"E117.right")])]})});
            var Q2;
            Q2=makeQuery(id+"F49.boolean.opBoolean","COPY",EDGE,{"derivedFrom":makeQuery(id+"F49.opExtrude","SWEPT_EDGE",EDGE,{"disambiguationData":[OSD([sQuery(id+"F48.wireOp",EDGE,"E117.bottom"),sQuery(id+"F48.wireOp",EDGE,"E117.left")])]})});
            var Q3;
            Q3=makeQuery(id+"F49.boolean.opBoolean","COPY",EDGE,{"derivedFrom":makeQuery(id+"F49.opExtrude","SWEPT_EDGE",EDGE,{"disambiguationData":[OSD([sQuery(id+"F48.wireOp",EDGE,"E117.top"),sQuery(id+"F48.wireOp",EDGE,"E117.left")])]})});
            fillet(context, id + "F86", {"entities" : qUnion([Q0, Q1, Q2, Q3]), "radius" : 2 * mm, "tangentPropagation" : true, "allowEdgeOverflow" : false});
        }
        {
            var Q0;
            Q0=makeQuery(id+"F47.boolean.opBoolean","COPY",EDGE,{"derivedFrom":makeQuery(id+"F47.opExtrude","SWEPT_EDGE",EDGE,{"disambiguationData":[OSD([sQuery(id+"F46.wireOp",EDGE,"E115.bottom"),sQuery(id+"F46.wireOp",EDGE,"E115.right")])]})});
            var Q1;
            Q1=makeQuery(id+"F47.boolean.opBoolean","COPY",EDGE,{"derivedFrom":makeQuery(id+"F47.opExtrude","SWEPT_EDGE",EDGE,{"disambiguationData":[OSD([sQuery(id+"F46.wireOp",EDGE,"E115.bottom"),sQuery(id+"F46.wireOp",EDGE,"E115.left")])]})});
            var Q2;
            Q2=makeQuery(id+"F47.boolean.opBoolean","COPY",EDGE,{"derivedFrom":makeQuery(id+"F47.opExtrude","SWEPT_EDGE",EDGE,{"disambiguationData":[OSD([sQuery(id+"F46.wireOp",EDGE,"E115.top"),sQuery(id+"F46.wireOp",EDGE,"E115.left")])]})});
            var Q3;
            Q3=makeQuery(id+"F47.boolean.opBoolean","COPY",EDGE,{"derivedFrom":makeQuery(id+"F47.opExtrude","SWEPT_EDGE",EDGE,{"disambiguationData":[OSD([sQuery(id+"F46.wireOp",EDGE,"E115.top"),sQuery(id+"F46.wireOp",EDGE,"E115.right")])]})});
            fillet(context, id + "F87", {"entities" : qUnion([Q0, Q1, Q2, Q3]), "radius" : 2 * mm, "tangentPropagation" : true, "allowEdgeOverflow" : false});
        }
        {
            var Q0;
            Q0=makeQuery(id+"F49.boolean.opBoolean","COPY",EDGE,{"derivedFrom":makeQuery(id+"F49.opExtrude","SWEPT_EDGE",EDGE,{"disambiguationData":[OSD([sQuery(id+"F48.wireOp",EDGE,"E118.bottom"),sQuery(id+"F48.wireOp",EDGE,"E118.left")])]})});
            var Q1;
            Q1=makeQuery(id+"F49.boolean.opBoolean","COPY",EDGE,{"derivedFrom":makeQuery(id+"F49.opExtrude","SWEPT_EDGE",EDGE,{"disambiguationData":[OSD([sQuery(id+"F48.wireOp",EDGE,"E118.top"),sQuery(id+"F48.wireOp",EDGE,"E118.left")])]})});
            var Q2;
            Q2=makeQuery(id+"F49.boolean.opBoolean","COPY",EDGE,{"derivedFrom":makeQuery(id+"F49.opExtrude","SWEPT_EDGE",EDGE,{"disambiguationData":[OSD([sQuery(id+"F48.wireOp",EDGE,"E118.bottom"),sQuery(id+"F48.wireOp",EDGE,"E118.right")])]})});
            var Q3;
            Q3=makeQuery(id+"F49.boolean.opBoolean","COPY",EDGE,{"derivedFrom":makeQuery(id+"F49.opExtrude","SWEPT_EDGE",EDGE,{"disambiguationData":[OSD([sQuery(id+"F48.wireOp",EDGE,"E118.top"),sQuery(id+"F48.wireOp",EDGE,"E118.right")])]})});
            fillet(context, id + "F88", {"entities" : qUnion([Q0, Q1, Q2, Q3]), "radius" : 2 * mm, "tangentPropagation" : true, "allowEdgeOverflow" : false});
        }
        {
            var Q0;
            {var subQ0=sQuery(id+"F58.wireOp",EDGE,"E123.bottom");var subQ1=sQuery(id+"F58.wireOp",EDGE,"E123.right");Q0=makeQuery(id+"F59.boolean.opBoolean","COPY",EDGE,{"disambiguationData":[TD([makeQuery(id+"F25.opExtrude","SWEPT_FACE",FACE,{"disambiguationData":[OSD([sQuery(id+"F24.wireOp",EDGE,"E62.left")])]})])],"derivedFrom":makeQuery(id+"F59.opExtrude","SWEPT_EDGE",EDGE,{"disambiguationData":[OSD([subQ0,subQ1])]})});}
            var Q1;
            {var subQ0=sQuery(id+"F58.wireOp",EDGE,"E123.right");var subQ1=sQuery(id+"F58.wireOp",EDGE,"E123.top");Q1=makeQuery(id+"F59.boolean.opBoolean","COPY",EDGE,{"disambiguationData":[TD([makeQuery(id+"F25.opExtrude","SWEPT_FACE",FACE,{"disambiguationData":[OSD([sQuery(id+"F24.wireOp",EDGE,"E62.left")])]})])],"derivedFrom":makeQuery(id+"F59.opExtrude","SWEPT_EDGE",EDGE,{"disambiguationData":[OSD([subQ1,subQ0])]})});}
            var Q2;
            {var subQ0=sQuery(id+"F58.wireOp",EDGE,"E123.left");var subQ1=sQuery(id+"F58.wireOp",EDGE,"E123.bottom");Q2=makeQuery(id+"F59.boolean.opBoolean","COPY",EDGE,{"disambiguationData":[TD([makeQuery(id+"F25.opExtrude","SWEPT_FACE",FACE,{"disambiguationData":[OSD([sQuery(id+"F24.wireOp",EDGE,"E62.left")])]})])],"derivedFrom":makeQuery(id+"F59.opExtrude","SWEPT_EDGE",EDGE,{"disambiguationData":[OSD([subQ1,subQ0])]})});}
            var Q3;
            {var subQ0=sQuery(id+"F58.wireOp",EDGE,"E123.left");var subQ1=sQuery(id+"F58.wireOp",EDGE,"E123.top");Q3=makeQuery(id+"F59.boolean.opBoolean","COPY",EDGE,{"disambiguationData":[TD([makeQuery(id+"F25.opExtrude","SWEPT_FACE",FACE,{"disambiguationData":[OSD([sQuery(id+"F24.wireOp",EDGE,"E62.left")])]})])],"derivedFrom":makeQuery(id+"F59.opExtrude","SWEPT_EDGE",EDGE,{"disambiguationData":[OSD([subQ1,subQ0])]})});}
            fillet(context, id + "F89", {"entities" : qUnion([Q0, Q1, Q2, Q3]), "radius" : 4 * mm, "tangentPropagation" : true, "allowEdgeOverflow" : false});
        }
        {
            var Q0;
            {var subQ0=sQuery(id+"F58.wireOp",EDGE,"E123.bottom");var subQ1=sQuery(id+"F58.wireOp",EDGE,"E123.right");Q0=makeQuery(id+"F59.boolean.opBoolean","COPY",EDGE,{"disambiguationData":[TD([makeQuery(id+"F25.opExtrude","SWEPT_FACE",FACE,{"disambiguationData":[OSD([sQuery(id+"F24.wireOp",EDGE,"E63.left")])]})])],"derivedFrom":makeQuery(id+"F59.opExtrude","SWEPT_EDGE",EDGE,{"disambiguationData":[OSD([subQ0,subQ1])]})});}
            var Q1;
            {var subQ0=sQuery(id+"F58.wireOp",EDGE,"E123.right");var subQ1=sQuery(id+"F58.wireOp",EDGE,"E123.top");Q1=makeQuery(id+"F59.boolean.opBoolean","COPY",EDGE,{"disambiguationData":[TD([makeQuery(id+"F25.opExtrude","SWEPT_FACE",FACE,{"disambiguationData":[OSD([sQuery(id+"F24.wireOp",EDGE,"E63.left")])]})])],"derivedFrom":makeQuery(id+"F59.opExtrude","SWEPT_EDGE",EDGE,{"disambiguationData":[OSD([subQ1,subQ0])]})});}
            var Q2;
            {var subQ0=sQuery(id+"F58.wireOp",EDGE,"E123.top");var subQ1=sQuery(id+"F58.wireOp",EDGE,"E123.left");Q2=makeQuery(id+"F59.boolean.opBoolean","COPY",EDGE,{"disambiguationData":[TD([makeQuery(id+"F25.opExtrude","SWEPT_FACE",FACE,{"disambiguationData":[OSD([sQuery(id+"F24.wireOp",EDGE,"E63.left")])]})])],"derivedFrom":makeQuery(id+"F59.opExtrude","SWEPT_EDGE",EDGE,{"disambiguationData":[OSD([subQ0,subQ1])]})});}
            var Q3;
            {var subQ0=sQuery(id+"F58.wireOp",EDGE,"E123.bottom");var subQ1=sQuery(id+"F58.wireOp",EDGE,"E123.left");Q3=makeQuery(id+"F59.boolean.opBoolean","COPY",EDGE,{"disambiguationData":[TD([makeQuery(id+"F25.opExtrude","SWEPT_FACE",FACE,{"disambiguationData":[OSD([sQuery(id+"F24.wireOp",EDGE,"E63.left")])]})])],"derivedFrom":makeQuery(id+"F59.opExtrude","SWEPT_EDGE",EDGE,{"disambiguationData":[OSD([subQ0,subQ1])]})});}
            fillet(context, id + "F90", {"entities" : qUnion([Q0, Q1, Q2, Q3]), "radius" : 2 * mm, "tangentPropagation" : true, "allowEdgeOverflow" : false});
        }
        {
            var Q0;
            Q0=makeQuery(id+"F37.boolean.opBoolean","COPY",EDGE,{"derivedFrom":makeQuery(id+"F37.opExtrude","SWEPT_EDGE",EDGE,{"disambiguationData":[OSD([sQuery(id+"F36.wireOp",EDGE,"E105.top"),sQuery(id+"F36.wireOp",EDGE,"E105.left")])]})});
            var Q1;
            Q1=makeQuery(id+"F37.boolean.opBoolean","COPY",EDGE,{"derivedFrom":makeQuery(id+"F37.opExtrude","SWEPT_EDGE",EDGE,{"disambiguationData":[OSD([sQuery(id+"F36.wireOp",EDGE,"E105.bottom"),sQuery(id+"F36.wireOp",EDGE,"E105.left")])]})});
            var Q2;
            Q2=makeQuery(id+"F37.boolean.opBoolean","COPY",EDGE,{"derivedFrom":makeQuery(id+"F37.opExtrude","SWEPT_EDGE",EDGE,{"disambiguationData":[OSD([sQuery(id+"F36.wireOp",EDGE,"E105.bottom"),sQuery(id+"F36.wireOp",EDGE,"E105.right")])]})});
            var Q3;
            Q3=makeQuery(id+"F37.boolean.opBoolean","COPY",EDGE,{"derivedFrom":makeQuery(id+"F37.opExtrude","SWEPT_EDGE",EDGE,{"disambiguationData":[OSD([sQuery(id+"F36.wireOp",EDGE,"E105.top"),sQuery(id+"F36.wireOp",EDGE,"E105.right")])]})});
            fillet(context, id + "F91", {"entities" : qUnion([Q0, Q1, Q2, Q3]), "radius" : 2 * mm, "tangentPropagation" : true, "allowEdgeOverflow" : false});
        }
        {
            var Q0;
            Q0=makeQuery(id+"F25.opExtrude","CAP_EDGE",EDGE,{"disambiguationData":[OSD([sQuery(id+"F24.wireOp",EDGE,"E64.top")])],"isStart":true});
            fillet(context, id + "F92", {"entities" : qUnion([Q0]), "radius" : 3 * mm, "tangentPropagation" : true, "allowEdgeOverflow" : false});
        }
        {
            var Q0;
            Q0=makeQuery(id+"F31.opExtrude","CAP_EDGE",EDGE,{"disambiguationData":[OSD([sQuery(id+"F30.wireOp",EDGE,"E70.top")])],"isStart":false});
            fillet(context, id + "F93", {"entities" : qUnion([Q0]), "radius" : 3 * mm, "tangentPropagation" : true, "allowEdgeOverflow" : false});
        }
        {
            var Q0;
            Q0=makeQuery(id+"F37.boolean.opBoolean","COPY",EDGE,{"derivedFrom":makeQuery(id+"F37.opExtrude","SWEPT_EDGE",EDGE,{"disambiguationData":[OSD([sQuery(id+"F36.wireOp",EDGE,"E104.top"),sQuery(id+"F36.wireOp",EDGE,"E104.right")])]})});
            var Q1;
            Q1=makeQuery(id+"F37.boolean.opBoolean","COPY",EDGE,{"derivedFrom":makeQuery(id+"F37.opExtrude","SWEPT_EDGE",EDGE,{"disambiguationData":[OSD([sQuery(id+"F36.wireOp",EDGE,"E104.bottom"),sQuery(id+"F36.wireOp",EDGE,"E104.right")])]})});
            var Q2;
            Q2=makeQuery(id+"F37.boolean.opBoolean","COPY",EDGE,{"derivedFrom":makeQuery(id+"F37.opExtrude","SWEPT_EDGE",EDGE,{"disambiguationData":[OSD([sQuery(id+"F36.wireOp",EDGE,"E104.bottom"),sQuery(id+"F36.wireOp",EDGE,"E104.left")])]})});
            var Q3;
            Q3=makeQuery(id+"F37.boolean.opBoolean","COPY",EDGE,{"derivedFrom":makeQuery(id+"F37.opExtrude","SWEPT_EDGE",EDGE,{"disambiguationData":[OSD([sQuery(id+"F36.wireOp",EDGE,"E104.top"),sQuery(id+"F36.wireOp",EDGE,"E104.left")])]})});
            fillet(context, id + "F94", {"entities" : qUnion([Q0, Q1, Q2, Q3]), "radius" : 2 * mm, "tangentPropagation" : true, "allowEdgeOverflow" : false});
        }
        {
            var Q0;
            Q0=makeQuery(id+"F51.boolean.opBoolean","COPY",EDGE,{"derivedFrom":makeQuery(id+"F51.opExtrude","SWEPT_EDGE",EDGE,{"disambiguationData":[OSD([sQuery(id+"F50.wireOp",EDGE,"E119.top"),sQuery(id+"F50.wireOp",EDGE,"E119.left")])]})});
            var Q1;
            Q1=makeQuery(id+"F51.boolean.opBoolean","COPY",EDGE,{"derivedFrom":makeQuery(id+"F51.opExtrude","SWEPT_EDGE",EDGE,{"disambiguationData":[OSD([sQuery(id+"F50.wireOp",EDGE,"E119.bottom"),sQuery(id+"F50.wireOp",EDGE,"E119.left")])]})});
            var Q2;
            Q2=makeQuery(id+"F51.boolean.opBoolean","COPY",EDGE,{"derivedFrom":makeQuery(id+"F51.opExtrude","SWEPT_EDGE",EDGE,{"disambiguationData":[OSD([sQuery(id+"F50.wireOp",EDGE,"E119.bottom"),sQuery(id+"F50.wireOp",EDGE,"E119.right")])]})});
            var Q3;
            Q3=makeQuery(id+"F51.boolean.opBoolean","COPY",EDGE,{"derivedFrom":makeQuery(id+"F51.opExtrude","SWEPT_EDGE",EDGE,{"disambiguationData":[OSD([sQuery(id+"F50.wireOp",EDGE,"E119.top"),sQuery(id+"F50.wireOp",EDGE,"E119.right")])]})});
            fillet(context, id + "F95", {"entities" : qUnion([Q0, Q1, Q2, Q3]), "radius" : 2 * mm, "tangentPropagation" : true, "allowEdgeOverflow" : false});
        }
        {
            var Q0;
            Q0=makeQuery(id+"F53.boolean.opBoolean","COPY",EDGE,{"derivedFrom":makeQuery(id+"F53.opExtrude","SWEPT_EDGE",EDGE,{"disambiguationData":[OSD([sQuery(id+"F52.wireOp",EDGE,"E120.top"),sQuery(id+"F52.wireOp",EDGE,"E120.right")])]})});
            var Q1;
            Q1=makeQuery(id+"F53.boolean.opBoolean","COPY",EDGE,{"derivedFrom":makeQuery(id+"F53.opExtrude","SWEPT_EDGE",EDGE,{"disambiguationData":[OSD([sQuery(id+"F52.wireOp",EDGE,"E120.bottom"),sQuery(id+"F52.wireOp",EDGE,"E120.right")])]})});
            var Q2;
            Q2=makeQuery(id+"F53.boolean.opBoolean","COPY",EDGE,{"derivedFrom":makeQuery(id+"F53.opExtrude","SWEPT_EDGE",EDGE,{"disambiguationData":[OSD([sQuery(id+"F52.wireOp",EDGE,"E120.top"),sQuery(id+"F52.wireOp",EDGE,"E120.left")])]})});
            var Q3;
            Q3=makeQuery(id+"F53.boolean.opBoolean","COPY",EDGE,{"derivedFrom":makeQuery(id+"F53.opExtrude","SWEPT_EDGE",EDGE,{"disambiguationData":[OSD([sQuery(id+"F52.wireOp",EDGE,"E120.bottom"),sQuery(id+"F52.wireOp",EDGE,"E120.left")])]})});
            fillet(context, id + "F96", {"entities" : qUnion([Q0, Q1, Q2, Q3]), "radius" : 2 * mm, "tangentPropagation" : true, "allowEdgeOverflow" : false});
        }
        {
            var Q0;
            Q0=makeQuery(id+"F37.boolean.opBoolean","COPY",EDGE,{"derivedFrom":makeQuery(id+"F37.opExtrude","SWEPT_EDGE",EDGE,{"disambiguationData":[OSD([sQuery(id+"F36.wireOp",EDGE,"E103.top"),sQuery(id+"F36.wireOp",EDGE,"E103.left")])]})});
            var Q1;
            Q1=makeQuery(id+"F37.boolean.opBoolean","COPY",EDGE,{"derivedFrom":makeQuery(id+"F37.opExtrude","SWEPT_EDGE",EDGE,{"disambiguationData":[OSD([sQuery(id+"F36.wireOp",EDGE,"E103.top"),sQuery(id+"F36.wireOp",EDGE,"E103.right")])]})});
            var Q2;
            Q2=makeQuery(id+"F37.boolean.opBoolean","COPY",EDGE,{"derivedFrom":makeQuery(id+"F37.opExtrude","SWEPT_EDGE",EDGE,{"disambiguationData":[OSD([sQuery(id+"F36.wireOp",EDGE,"E103.bottom"),sQuery(id+"F36.wireOp",EDGE,"E103.right")])]})});
            var Q3;
            Q3=makeQuery(id+"F37.boolean.opBoolean","COPY",EDGE,{"derivedFrom":makeQuery(id+"F37.opExtrude","SWEPT_EDGE",EDGE,{"disambiguationData":[OSD([sQuery(id+"F36.wireOp",EDGE,"E103.bottom"),sQuery(id+"F36.wireOp",EDGE,"E103.left")])]})});
            fillet(context, id + "F97", {"entities" : qUnion([Q0, Q1, Q2, Q3]), "radius" : 2 * mm, "tangentPropagation" : true, "allowEdgeOverflow" : false});
        }
        {
            var Q0;
            Q0=makeQuery(id+"F55.boolean.opBoolean","COPY",EDGE,{"derivedFrom":makeQuery(id+"F55.opExtrude","SWEPT_EDGE",EDGE,{"disambiguationData":[OSD([sQuery(id+"F54.wireOp",EDGE,"E121.bottom"),sQuery(id+"F54.wireOp",EDGE,"E121.right")])]})});
            var Q1;
            Q1=makeQuery(id+"F55.boolean.opBoolean","COPY",EDGE,{"derivedFrom":makeQuery(id+"F55.opExtrude","SWEPT_EDGE",EDGE,{"disambiguationData":[OSD([sQuery(id+"F54.wireOp",EDGE,"E121.bottom"),sQuery(id+"F54.wireOp",EDGE,"E121.left")])]})});
            var Q2;
            Q2=makeQuery(id+"F55.boolean.opBoolean","COPY",EDGE,{"derivedFrom":makeQuery(id+"F55.opExtrude","SWEPT_EDGE",EDGE,{"disambiguationData":[OSD([sQuery(id+"F54.wireOp",EDGE,"E121.top"),sQuery(id+"F54.wireOp",EDGE,"E121.right")])]})});
            var Q3;
            Q3=makeQuery(id+"F55.boolean.opBoolean","COPY",EDGE,{"derivedFrom":makeQuery(id+"F55.opExtrude","SWEPT_EDGE",EDGE,{"disambiguationData":[OSD([sQuery(id+"F54.wireOp",EDGE,"E121.top"),sQuery(id+"F54.wireOp",EDGE,"E121.left")])]})});
            fillet(context, id + "F98", {"entities" : qUnion([Q0, Q1, Q2, Q3]), "radius" : 2 * mm, "tangentPropagation" : true, "allowEdgeOverflow" : false});
        }
        {
            var Q0;
            {var subQ0=sQuery(id+"F10.wireOp",EDGE,"E23.right");var subQ1=sQuery(id+"F10.wireOp",EDGE,"E23.left");var subQ2=sQuery(id+"F10.wireOp",EDGE,"E23.top");var subQ3=sQuery(id+"F10.wireOp",EDGE,"E23.bottom");var subQ4=sQuery(id+"F44.wireOp",EDGE,"E112.top");var subQ5=sQuery(id+"F44.wireOp",EDGE,"E112.left");Q0=makeQuery(id+"F45.boolean.opBoolean","COPY",EDGE,{"disambiguationData":[TD([makeQuery(id+"F11.opExtrude","CAP_FACE",FACE,{"disambiguationData":[OSD([subQ3,subQ2,subQ1,subQ0])],"isStart":true})])],"derivedFrom":makeQuery(id+"F45.opExtrude","SWEPT_EDGE",EDGE,{"disambiguationData":[OSD([subQ4,subQ5])]})});}
            var Q1;
            {var subQ0=sQuery(id+"F10.wireOp",EDGE,"E23.right");var subQ1=sQuery(id+"F10.wireOp",EDGE,"E23.left");var subQ2=sQuery(id+"F10.wireOp",EDGE,"E23.top");var subQ3=sQuery(id+"F10.wireOp",EDGE,"E23.bottom");var subQ4=sQuery(id+"F44.wireOp",EDGE,"E112.right");var subQ5=sQuery(id+"F44.wireOp",EDGE,"E112.top");Q1=makeQuery(id+"F45.boolean.opBoolean","COPY",EDGE,{"disambiguationData":[TD([makeQuery(id+"F11.opExtrude","CAP_FACE",FACE,{"disambiguationData":[OSD([subQ3,subQ2,subQ1,subQ0])],"isStart":true})])],"derivedFrom":makeQuery(id+"F45.opExtrude","SWEPT_EDGE",EDGE,{"disambiguationData":[OSD([subQ5,subQ4])]})});}
            var Q2;
            {var subQ0=sQuery(id+"F10.wireOp",EDGE,"E23.right");var subQ1=sQuery(id+"F10.wireOp",EDGE,"E23.left");var subQ2=sQuery(id+"F10.wireOp",EDGE,"E23.top");var subQ3=sQuery(id+"F10.wireOp",EDGE,"E23.bottom");var subQ4=sQuery(id+"F44.wireOp",EDGE,"E112.bottom");var subQ5=sQuery(id+"F44.wireOp",EDGE,"E112.left");Q2=makeQuery(id+"F45.boolean.opBoolean","COPY",EDGE,{"disambiguationData":[TD([makeQuery(id+"F11.opExtrude","CAP_FACE",FACE,{"disambiguationData":[OSD([subQ3,subQ2,subQ1,subQ0])],"isStart":true})])],"derivedFrom":makeQuery(id+"F45.opExtrude","SWEPT_EDGE",EDGE,{"disambiguationData":[OSD([subQ4,subQ5])]})});}
            var Q3;
            {var subQ0=sQuery(id+"F10.wireOp",EDGE,"E23.right");var subQ1=sQuery(id+"F10.wireOp",EDGE,"E23.left");var subQ2=sQuery(id+"F10.wireOp",EDGE,"E23.top");var subQ3=sQuery(id+"F10.wireOp",EDGE,"E23.bottom");var subQ4=sQuery(id+"F44.wireOp",EDGE,"E112.bottom");var subQ5=sQuery(id+"F44.wireOp",EDGE,"E112.right");Q3=makeQuery(id+"F45.boolean.opBoolean","COPY",EDGE,{"disambiguationData":[TD([makeQuery(id+"F11.opExtrude","CAP_FACE",FACE,{"disambiguationData":[OSD([subQ3,subQ2,subQ1,subQ0])],"isStart":true})])],"derivedFrom":makeQuery(id+"F45.opExtrude","SWEPT_EDGE",EDGE,{"disambiguationData":[OSD([subQ4,subQ5])]})});}
            fillet(context, id + "F99", {"entities" : qUnion([Q0, Q1, Q2, Q3]), "radius" : 2 * mm, "tangentPropagation" : true, "allowEdgeOverflow" : false});
        }
        {
            var Q0;
            Q0=makeQuery(id+"F9.opExtrude","SWEPT_EDGE",EDGE,{"disambiguationData":[OSD([sQuery(id+"F0.wireOp",EDGE,"E2"),sQuery(id+"F8.wireOp",EDGE,"E21.top"),sQuery(id+"F8.wireOp",EDGE,"E21.left")])]});
            fillet(context, id + "F100", {"entities" : qUnion([Q0]), "radius" : 3 * mm, "tangentPropagation" : true, "allowEdgeOverflow" : false});
        }
        {
            var Q0;
            Q0=makeQuery(id+"F43.boolean.opBoolean","COPY",EDGE,{"derivedFrom":makeQuery(id+"F43.opExtrude","SWEPT_EDGE",EDGE,{"disambiguationData":[OSD([sQuery(id+"F42.wireOp",EDGE,"E109.bottom"),sQuery(id+"F42.wireOp",EDGE,"E109.right")])]})});
            var Q1;
            Q1=makeQuery(id+"F43.boolean.opBoolean","COPY",EDGE,{"derivedFrom":makeQuery(id+"F43.opExtrude","SWEPT_EDGE",EDGE,{"disambiguationData":[OSD([sQuery(id+"F42.wireOp",EDGE,"E109.bottom"),sQuery(id+"F42.wireOp",EDGE,"E109.left")])]})});
            var Q2;
            Q2=makeQuery(id+"F43.boolean.opBoolean","COPY",EDGE,{"derivedFrom":makeQuery(id+"F43.opExtrude","SWEPT_EDGE",EDGE,{"disambiguationData":[OSD([sQuery(id+"F42.wireOp",EDGE,"E109.top"),sQuery(id+"F42.wireOp",EDGE,"E109.left")])]})});
            var Q3;
            Q3=makeQuery(id+"F43.boolean.opBoolean","COPY",EDGE,{"derivedFrom":makeQuery(id+"F43.opExtrude","SWEPT_EDGE",EDGE,{"disambiguationData":[OSD([sQuery(id+"F42.wireOp",EDGE,"E109.top"),sQuery(id+"F42.wireOp",EDGE,"E109.right")])]})});
            fillet(context, id + "F101", {"entities" : qUnion([Q0, Q1, Q2, Q3]), "radius" : 2 * mm, "tangentPropagation" : true, "allowEdgeOverflow" : false});
        }
        {
            var Q0;
            {var subQ0=sQuery(id+"F13.wireOp",EDGE,"E24.right");var subQ1=sQuery(id+"F13.wireOp",EDGE,"E24.left");var subQ2=sQuery(id+"F13.wireOp",EDGE,"E24.top");var subQ3=sQuery(id+"F13.wireOp",EDGE,"E24.bottom");var subQ4=sQuery(id+"F44.wireOp",EDGE,"E112.right");var subQ5=sQuery(id+"F44.wireOp",EDGE,"E112.top");Q0=makeQuery(id+"F45.boolean.opBoolean","COPY",EDGE,{"disambiguationData":[TD([makeQuery(id+"F14.opExtrude","CAP_FACE",FACE,{"disambiguationData":[OSD([subQ3,subQ2,subQ1,subQ0])],"isStart":true})])],"derivedFrom":makeQuery(id+"F45.opExtrude","SWEPT_EDGE",EDGE,{"disambiguationData":[OSD([subQ5,subQ4])]})});}
            var Q1;
            {var subQ0=sQuery(id+"F13.wireOp",EDGE,"E24.right");var subQ1=sQuery(id+"F13.wireOp",EDGE,"E24.left");var subQ2=sQuery(id+"F13.wireOp",EDGE,"E24.top");var subQ3=sQuery(id+"F13.wireOp",EDGE,"E24.bottom");var subQ4=sQuery(id+"F44.wireOp",EDGE,"E112.bottom");var subQ5=sQuery(id+"F44.wireOp",EDGE,"E112.right");Q1=makeQuery(id+"F45.boolean.opBoolean","COPY",EDGE,{"disambiguationData":[TD([makeQuery(id+"F14.opExtrude","CAP_FACE",FACE,{"disambiguationData":[OSD([subQ3,subQ2,subQ1,subQ0])],"isStart":true})])],"derivedFrom":makeQuery(id+"F45.opExtrude","SWEPT_EDGE",EDGE,{"disambiguationData":[OSD([subQ4,subQ5])]})});}
            var Q2;
            {var subQ0=sQuery(id+"F13.wireOp",EDGE,"E24.right");var subQ1=sQuery(id+"F13.wireOp",EDGE,"E24.left");var subQ2=sQuery(id+"F13.wireOp",EDGE,"E24.top");var subQ3=sQuery(id+"F13.wireOp",EDGE,"E24.bottom");var subQ4=sQuery(id+"F44.wireOp",EDGE,"E112.bottom");var subQ5=sQuery(id+"F44.wireOp",EDGE,"E112.left");Q2=makeQuery(id+"F45.boolean.opBoolean","COPY",EDGE,{"disambiguationData":[TD([makeQuery(id+"F14.opExtrude","CAP_FACE",FACE,{"disambiguationData":[OSD([subQ3,subQ2,subQ1,subQ0])],"isStart":true})])],"derivedFrom":makeQuery(id+"F45.opExtrude","SWEPT_EDGE",EDGE,{"disambiguationData":[OSD([subQ4,subQ5])]})});}
            var Q3;
            {var subQ0=sQuery(id+"F13.wireOp",EDGE,"E24.right");var subQ1=sQuery(id+"F13.wireOp",EDGE,"E24.left");var subQ2=sQuery(id+"F13.wireOp",EDGE,"E24.top");var subQ3=sQuery(id+"F13.wireOp",EDGE,"E24.bottom");var subQ4=sQuery(id+"F44.wireOp",EDGE,"E112.top");var subQ5=sQuery(id+"F44.wireOp",EDGE,"E112.left");Q3=makeQuery(id+"F45.boolean.opBoolean","COPY",EDGE,{"disambiguationData":[TD([makeQuery(id+"F14.opExtrude","CAP_FACE",FACE,{"disambiguationData":[OSD([subQ3,subQ2,subQ1,subQ0])],"isStart":true})])],"derivedFrom":makeQuery(id+"F45.opExtrude","SWEPT_EDGE",EDGE,{"disambiguationData":[OSD([subQ4,subQ5])]})});}
            fillet(context, id + "F102", {"entities" : qUnion([Q0, Q1, Q2, Q3]), "radius" : 2 * mm, "tangentPropagation" : true, "allowEdgeOverflow" : false});
        }
        {
            var Q0;
            Q0=makeQuery(id+"F57.boolean.opBoolean","COPY",EDGE,{"derivedFrom":makeQuery(id+"F57.opExtrude","SWEPT_EDGE",EDGE,{"disambiguationData":[OSD([sQuery(id+"F56.wireOp",EDGE,"E122.top"),sQuery(id+"F56.wireOp",EDGE,"E122.left")])]})});
            var Q1;
            Q1=makeQuery(id+"F57.boolean.opBoolean","COPY",EDGE,{"derivedFrom":makeQuery(id+"F57.opExtrude","SWEPT_EDGE",EDGE,{"disambiguationData":[OSD([sQuery(id+"F56.wireOp",EDGE,"E122.bottom"),sQuery(id+"F56.wireOp",EDGE,"E122.left")])]})});
            var Q2;
            Q2=makeQuery(id+"F57.boolean.opBoolean","COPY",EDGE,{"derivedFrom":makeQuery(id+"F57.opExtrude","SWEPT_EDGE",EDGE,{"disambiguationData":[OSD([sQuery(id+"F56.wireOp",EDGE,"E122.bottom"),sQuery(id+"F56.wireOp",EDGE,"E122.right")])]})});
            var Q3;
            Q3=makeQuery(id+"F57.boolean.opBoolean","COPY",EDGE,{"derivedFrom":makeQuery(id+"F57.opExtrude","SWEPT_EDGE",EDGE,{"disambiguationData":[OSD([sQuery(id+"F56.wireOp",EDGE,"E122.top"),sQuery(id+"F56.wireOp",EDGE,"E122.right")])]})});
            fillet(context, id + "F103", {"entities" : qUnion([Q0, Q1, Q2, Q3]), "radius" : 2 * mm, "tangentPropagation" : true, "allowEdgeOverflow" : false});
        }
        {
            var Q0;
            Q0=makeQuery(id+"F9.opExtrude","SWEPT_EDGE",EDGE,{"disambiguationData":[OSD([sQuery(id+"F0.wireOp",EDGE,"E2"),sQuery(id+"F8.wireOp",EDGE,"E22.top"),sQuery(id+"F8.wireOp",EDGE,"E22.left")])]});
            fillet(context, id + "F104", {"entities" : qUnion([Q0]), "radius" : 3 * mm, "tangentPropagation" : true, "allowEdgeOverflow" : false});
        }
        {
            var Q0;
            Q0=makeQuery(id+"F43.boolean.opBoolean","COPY",EDGE,{"derivedFrom":makeQuery(id+"F43.opExtrude","SWEPT_EDGE",EDGE,{"disambiguationData":[OSD([sQuery(id+"F42.wireOp",EDGE,"E110.top"),sQuery(id+"F42.wireOp",EDGE,"E110.right")])]})});
            var Q1;
            Q1=makeQuery(id+"F43.boolean.opBoolean","COPY",EDGE,{"derivedFrom":makeQuery(id+"F43.opExtrude","SWEPT_EDGE",EDGE,{"disambiguationData":[OSD([sQuery(id+"F42.wireOp",EDGE,"E110.top"),sQuery(id+"F42.wireOp",EDGE,"E110.left")])]})});
            var Q2;
            Q2=makeQuery(id+"F43.boolean.opBoolean","COPY",EDGE,{"derivedFrom":makeQuery(id+"F43.opExtrude","SWEPT_EDGE",EDGE,{"disambiguationData":[OSD([sQuery(id+"F42.wireOp",EDGE,"E110.bottom"),sQuery(id+"F42.wireOp",EDGE,"E110.left")])]})});
            var Q3;
            Q3=makeQuery(id+"F43.boolean.opBoolean","COPY",EDGE,{"derivedFrom":makeQuery(id+"F43.opExtrude","SWEPT_EDGE",EDGE,{"disambiguationData":[OSD([sQuery(id+"F42.wireOp",EDGE,"E110.bottom"),sQuery(id+"F42.wireOp",EDGE,"E110.right")])]})});
            fillet(context, id + "F105", {"entities" : qUnion([Q0, Q1, Q2, Q3]), "radius" : 2 * mm, "tangentPropagation" : true, "allowEdgeOverflow" : false});
        }
        {
            var Q0;
            {var subQ0=sQuery(id+"F16.wireOp",EDGE,"E25.right");var subQ1=sQuery(id+"F16.wireOp",EDGE,"E25.left");var subQ2=sQuery(id+"F16.wireOp",EDGE,"E25.top");var subQ3=sQuery(id+"F16.wireOp",EDGE,"E25.bottom");var subQ4=sQuery(id+"F44.wireOp",EDGE,"E112.bottom");var subQ5=sQuery(id+"F44.wireOp",EDGE,"E112.right");Q0=makeQuery(id+"F45.boolean.opBoolean","COPY",EDGE,{"disambiguationData":[TD([makeQuery(id+"F17.opExtrude","CAP_FACE",FACE,{"disambiguationData":[OSD([subQ3,subQ2,subQ1,subQ0])],"isStart":true})])],"derivedFrom":makeQuery(id+"F45.opExtrude","SWEPT_EDGE",EDGE,{"disambiguationData":[OSD([subQ4,subQ5])]})});}
            var Q1;
            {var subQ0=sQuery(id+"F16.wireOp",EDGE,"E25.right");var subQ1=sQuery(id+"F16.wireOp",EDGE,"E25.left");var subQ2=sQuery(id+"F16.wireOp",EDGE,"E25.top");var subQ3=sQuery(id+"F16.wireOp",EDGE,"E25.bottom");var subQ4=sQuery(id+"F44.wireOp",EDGE,"E112.bottom");var subQ5=sQuery(id+"F44.wireOp",EDGE,"E112.left");Q1=makeQuery(id+"F45.boolean.opBoolean","COPY",EDGE,{"disambiguationData":[TD([makeQuery(id+"F17.opExtrude","CAP_FACE",FACE,{"disambiguationData":[OSD([subQ3,subQ2,subQ1,subQ0])],"isStart":true})])],"derivedFrom":makeQuery(id+"F45.opExtrude","SWEPT_EDGE",EDGE,{"disambiguationData":[OSD([subQ4,subQ5])]})});}
            var Q2;
            {var subQ0=sQuery(id+"F16.wireOp",EDGE,"E25.right");var subQ1=sQuery(id+"F16.wireOp",EDGE,"E25.left");var subQ2=sQuery(id+"F16.wireOp",EDGE,"E25.top");var subQ3=sQuery(id+"F16.wireOp",EDGE,"E25.bottom");var subQ4=sQuery(id+"F44.wireOp",EDGE,"E112.top");var subQ5=sQuery(id+"F44.wireOp",EDGE,"E112.left");Q2=makeQuery(id+"F45.boolean.opBoolean","COPY",EDGE,{"disambiguationData":[TD([makeQuery(id+"F17.opExtrude","CAP_FACE",FACE,{"disambiguationData":[OSD([subQ3,subQ2,subQ1,subQ0])],"isStart":true})])],"derivedFrom":makeQuery(id+"F45.opExtrude","SWEPT_EDGE",EDGE,{"disambiguationData":[OSD([subQ4,subQ5])]})});}
            var Q3;
            {var subQ0=sQuery(id+"F16.wireOp",EDGE,"E25.right");var subQ1=sQuery(id+"F16.wireOp",EDGE,"E25.left");var subQ2=sQuery(id+"F16.wireOp",EDGE,"E25.top");var subQ3=sQuery(id+"F16.wireOp",EDGE,"E25.bottom");var subQ4=sQuery(id+"F44.wireOp",EDGE,"E112.right");var subQ5=sQuery(id+"F44.wireOp",EDGE,"E112.top");Q3=makeQuery(id+"F45.boolean.opBoolean","COPY",EDGE,{"disambiguationData":[TD([makeQuery(id+"F17.opExtrude","CAP_FACE",FACE,{"disambiguationData":[OSD([subQ3,subQ2,subQ1,subQ0])],"isStart":true})])],"derivedFrom":makeQuery(id+"F45.opExtrude","SWEPT_EDGE",EDGE,{"disambiguationData":[OSD([subQ5,subQ4])]})});}
            fillet(context, id + "F106", {"entities" : qUnion([Q0, Q1, Q2, Q3]), "radius" : 2 * mm, "tangentPropagation" : true, "allowEdgeOverflow" : false});
        }
        {
            var Q0;
            Q0=makeQuery(id+"F43.boolean.opBoolean","COPY",EDGE,{"derivedFrom":makeQuery(id+"F43.opExtrude","SWEPT_EDGE",EDGE,{"disambiguationData":[OSD([sQuery(id+"F42.wireOp",EDGE,"E111.top"),sQuery(id+"F42.wireOp",EDGE,"E111.left")])]})});
            var Q1;
            Q1=makeQuery(id+"F43.boolean.opBoolean","COPY",EDGE,{"derivedFrom":makeQuery(id+"F43.opExtrude","SWEPT_EDGE",EDGE,{"disambiguationData":[OSD([sQuery(id+"F42.wireOp",EDGE,"E111.top"),sQuery(id+"F42.wireOp",EDGE,"E111.right")])]})});
            var Q2;
            Q2=makeQuery(id+"F43.boolean.opBoolean","COPY",EDGE,{"derivedFrom":makeQuery(id+"F43.opExtrude","SWEPT_EDGE",EDGE,{"disambiguationData":[OSD([sQuery(id+"F42.wireOp",EDGE,"E111.bottom"),sQuery(id+"F42.wireOp",EDGE,"E111.right")])]})});
            var Q3;
            Q3=makeQuery(id+"F43.boolean.opBoolean","COPY",EDGE,{"derivedFrom":makeQuery(id+"F43.opExtrude","SWEPT_EDGE",EDGE,{"disambiguationData":[OSD([sQuery(id+"F42.wireOp",EDGE,"E111.bottom"),sQuery(id+"F42.wireOp",EDGE,"E111.left")])]})});
            fillet(context, id + "F107", {"entities" : qUnion([Q0, Q1, Q2, Q3]), "radius" : 2 * mm, "tangentPropagation" : true, "allowEdgeOverflow" : false});
        }
        {
            var Q0;
            Q0=qCreatedBy(makeId("Right.planeOp"),FACE);
            var sketch = newSketch(context, id + "F108", { "sketchPlane" : qUnion([Q0])});
            skLineSegment(sketch, "E124.bottom", {"start": v(846, 4) * mm, "end": v(894, 4) * mm});
            skLineSegment(sketch, "E124.top", {"start": v(846, 56) * mm, "end": v(894, 56) * mm});
            skLineSegment(sketch, "E124.left", {"start": v(844, 6) * mm, "end": v(844, 54) * mm});
            skLineSegment(sketch, "E124.right", {"start": v(896, 6) * mm, "end": v(896, 54) * mm});
            skPoint(sketch, "E125.visualSharp", {"position": v(844, 56) * mm});
            skArc(sketch, "E125.filletArc", {"start": v(846, 56) * mm, "mid": v(844.59, 55.41) * mm, "end": v(844, 54) * mm});
            skPoint(sketch, "E126.visualSharp", {"position": v(896, 56) * mm});
            skArc(sketch, "E126.filletArc", {"start": v(896, 54) * mm, "mid": v(895.41, 55.41) * mm, "end": v(894, 56) * mm});
            skPoint(sketch, "E127.visualSharp", {"position": v(844, 4) * mm});
            skArc(sketch, "E127.filletArc", {"start": v(844, 6) * mm, "mid": v(844.59, 4.59) * mm, "end": v(846, 4) * mm});
            skPoint(sketch, "E128.visualSharp", {"position": v(896, 4) * mm});
            skArc(sketch, "E128.filletArc", {"start": v(894, 4) * mm, "mid": v(895.41, 4.59) * mm, "end": v(896, 6) * mm});
            skLineSegment(sketch, "E129.bottom", {"start": v(-894, 4) * mm, "end": v(-846, 4) * mm});
            skLineSegment(sketch, "E129.top", {"start": v(-894, 56) * mm, "end": v(-846, 56) * mm});
            skLineSegment(sketch, "E129.left", {"start": v(-896, 6) * mm, "end": v(-896, 54) * mm});
            skLineSegment(sketch, "E129.right", {"start": v(-844, 6) * mm, "end": v(-844, 54) * mm});
            skPoint(sketch, "E130.visualSharp", {"position": v(-896, 56) * mm});
            skArc(sketch, "E130.filletArc", {"start": v(-894, 56) * mm, "mid": v(-895.41, 55.41) * mm, "end": v(-896, 54) * mm});
            skPoint(sketch, "E131.visualSharp", {"position": v(-896, 4) * mm});
            skArc(sketch, "E131.filletArc", {"start": v(-896, 6) * mm, "mid": v(-895.41, 4.59) * mm, "end": v(-894, 4) * mm});
            skPoint(sketch, "E132.visualSharp", {"position": v(-844, 4) * mm});
            skArc(sketch, "E132.filletArc", {"start": v(-846, 4) * mm, "mid": v(-844.59, 4.59) * mm, "end": v(-844, 6) * mm});
            skPoint(sketch, "E133.visualSharp", {"position": v(-844, 56) * mm});
            skArc(sketch, "E133.filletArc", {"start": v(-844, 54) * mm, "mid": v(-844.59, 55.41) * mm, "end": v(-846, 56) * mm});
            skSolve(sketch);
        }
        {
            var Q0;
            Q0=makeQuery(id+"F43.boolean.opBoolean","COPY",EDGE,{"derivedFrom":makeQuery(id+"F43.opExtrude","SWEPT_EDGE",EDGE,{"disambiguationData":[OSD([sQuery(id+"F42.wireOp",EDGE,"E108.top"),sQuery(id+"F42.wireOp",EDGE,"E108.left")])]})});
            var Q1;
            Q1=makeQuery(id+"F43.boolean.opBoolean","COPY",EDGE,{"derivedFrom":makeQuery(id+"F43.opExtrude","SWEPT_EDGE",EDGE,{"disambiguationData":[OSD([sQuery(id+"F42.wireOp",EDGE,"E108.top"),sQuery(id+"F42.wireOp",EDGE,"E108.right")])]})});
            var Q2;
            Q2=makeQuery(id+"F43.boolean.opBoolean","COPY",EDGE,{"derivedFrom":makeQuery(id+"F43.opExtrude","SWEPT_EDGE",EDGE,{"disambiguationData":[OSD([sQuery(id+"F42.wireOp",EDGE,"E108.bottom"),sQuery(id+"F42.wireOp",EDGE,"E108.right")])]})});
            var Q3;
            Q3=makeQuery(id+"F43.boolean.opBoolean","COPY",EDGE,{"derivedFrom":makeQuery(id+"F43.opExtrude","SWEPT_EDGE",EDGE,{"disambiguationData":[OSD([sQuery(id+"F42.wireOp",EDGE,"E108.bottom"),sQuery(id+"F42.wireOp",EDGE,"E108.left")])]})});
            fillet(context, id + "F109", {"entities" : qUnion([Q0, Q1, Q2, Q3]), "radius" : 2 * mm, "tangentPropagation" : true, "allowEdgeOverflow" : false});
        }
        {
            var Q0;
            Q0 = qSketchRegion(id + "F108", true);
            extrude(context, id + "F110", {"entities" : qUnion([Q0]), "operationType" : NewBodyOperationType.REMOVE, "endBound" : BoundingType.SYMMETRIC, "depth" : 3000 * mm, "offsetDistance" : 25 * mm});
        }
    });
